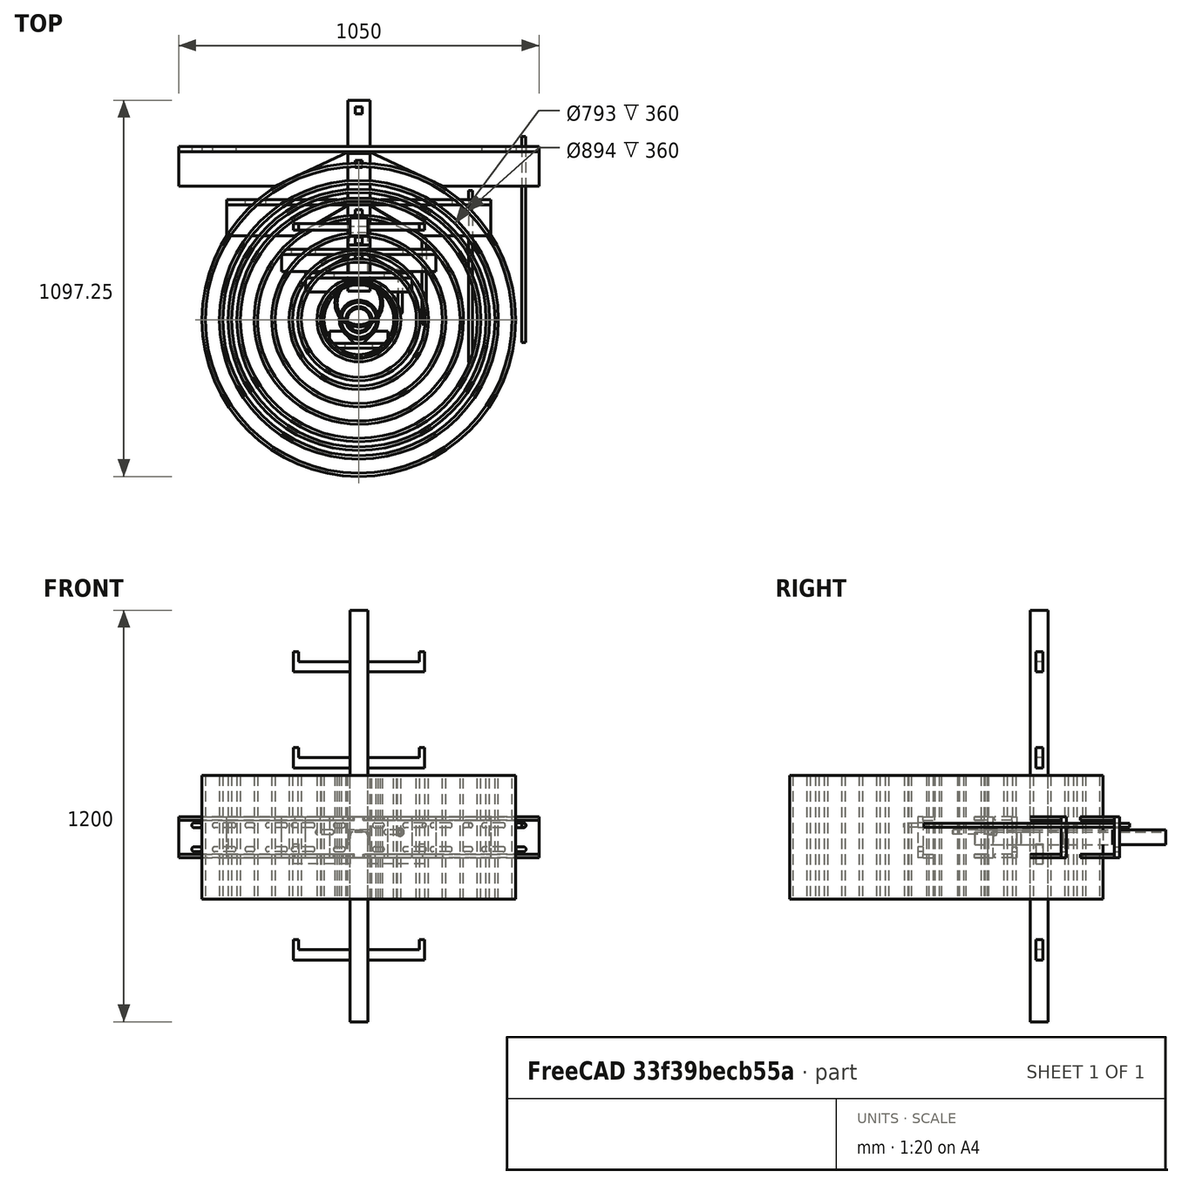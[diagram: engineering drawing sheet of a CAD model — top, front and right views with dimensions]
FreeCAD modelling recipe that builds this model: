
FCSTD DOCUMENT  (FreeCAD 0.21R33771 (Git))
Label: ladder_clamp
License: All rights reserved
LicenseURL: http://en.wikipedia.org/wiki/All_rights_reserved
objects: TechDraw::DrawViewDimension×53, Sketcher::SketchObject×26, Part::Extrusion×25, Part::FeaturePython×17, Part::Feature×15, Part::Cut×12, TechDraw::DrawProjGroupItem×12, App::DocumentObjectGroup×5, TechDraw::DrawSVGTemplate×4, TechDraw::DrawProjGroup×4, TechDraw::DrawViewBalloon×4, TechDraw::DrawViewAnnotation×4, TechDraw::DrawPage×4, Part::Cylinder×3, Fem::ConstraintForce×2, Part::MultiFuse×1, Fem::FemMeshObjectPython×1, Fem::FemSolverObjectPython×1, App::MaterialObjectPython×1, Fem::ConstraintFixed×1, +1 more types
note: 99 computed .brp shape members not serialized (recipe doc carries the construction recipe); baked Part::Feature solids carry a one-line shape summary decoded from their .brp

FEATURE [Part::Feature] BOLTS_part  label="Circular hollow profile 76.1/5.0 l=360.0"
  Placement = pos=(0,0,-120) rot=(0,0,1;0rad)
  shape: bbox 76.1 x 76.1 x 360 mm, 4 faces (baked)
FEATURE [Part::Feature] BOLTS_part001  label="Circular hollow profile 114.3/6.3 l=360.0"
  Placement = pos=(0,0,-120) rot=(0,0,1;0rad)
  shape: bbox 114.3 x 114.3 x 360 mm, 4 faces (baked)
FEATURE [Part::Feature] BOLTS_part002  label="Circular hollow profile 139.7/6.3 l=360.0"
  Placement = pos=(0,49,-120) rot=(0,0,1;0rad)
  shape: bbox 139.7 x 139.7 x 360 mm, 4 faces (baked)
FEATURE [Part::Feature] BOLTS_part003  label="Circular hollow profile 219.1/8.0 l=360.0"
  Placement = pos=(0,0,-120) rot=(0,0,1;0rad)
  shape: bbox 219.1 x 219.1 x 360 mm, 4 faces (baked)
FEATURE [Part::Feature] BOLTS_part004  label="Circular hollow profile 244.5/10.0 l=360.0"
  Placement = pos=(0,0,-120) rot=(0,0,1;0rad)
  shape: bbox 244.5 x 244.5 x 360 mm, 4 faces (baked)
FEATURE [Part::Feature] BOLTS_part005  label="Circular hollow profile 355.6/10.0 l=360.0"
  Placement = pos=(0,0,-120) rot=(0,0,1;0rad)
  shape: bbox 355.6 x 355.6 x 360 mm, 4 faces (baked)
FEATURE [Part::Feature] BOLTS_part006  label="Circular hollow profile 406.4/10.0 l=360.0"
  Placement = pos=(0,0,-120) rot=(0,0,1;0rad)
  shape: bbox 406.4 x 406.4 x 360 mm, 4 faces (baked)
FEATURE [Part::Feature] BOLTS_part007  label="Circular hollow profile 610.0/10.0 l=360.0"
  Placement = pos=(0,0,-120) rot=(0,0,1;0rad)
  shape: bbox 610 x 610 x 360 mm, 4 faces (baked)
FEATURE [Part::Feature] BOLTS_part008  label="Circular hollow profile 914.0/10.0 l=360.0"
  Placement = pos=(0,0,-120) rot=(0,0,1;0rad)
  shape: bbox 914 x 914 x 360 mm, 4 faces (baked)
FEATURE [Sketcher::SketchObject] Sketch
  FullyConstrained = true
  sketch-geometry (10):
    g0: Circle CenterX=0 CenterY=0 CenterZ=0 NormalX=0 NormalY=0 NormalZ=1 AngleXU=0 Radius=57.15
    g1: LineSegment StartX=-47.5 StartY=33.3223 StartZ=0 EndX=-12.5 EndY=68.3223 EndZ=0
    g2: LineSegment StartX=12.5 StartY=68.3223 StartZ=0 EndX=47.5 EndY=33.3223 EndZ=0
    g3: LineSegment StartX=-12.5 StartY=68.3223 StartZ=0 EndX=12.5 EndY=68.3223 EndZ=0
    g4: LineSegment StartX=47.5 StartY=33.3223 StartZ=0 EndX=85 EndY=33.3223 EndZ=0
    g5: LineSegment StartX=85 StartY=33.3223 StartZ=0 EndX=85 EndY=68.3223 EndZ=0
    g6: LineSegment StartX=85 StartY=68.3223 StartZ=0 EndX=12.5 EndY=68.3223 EndZ=0
    g7: LineSegment StartX=-12.5 StartY=68.3223 StartZ=0 EndX=-85 EndY=68.3223 EndZ=0
    g8: LineSegment StartX=-85 StartY=68.3223 StartZ=0 EndX=-85 EndY=33.3223 EndZ=0
    g9: LineSegment StartX=-85 StartY=33.3223 StartZ=0 EndX=-47.5 EndY=33.3223 EndZ=0
  constraints (26):
    c: Coincident(g0,g-1)
    c: Tangent(g1,g0)
    c: Symmetric(g1,g2,g-2)
    c: Symmetric(g1,g2,g-2)
    c: Coincident(g3,g1)
    c: Coincident(g3,g2)
    c: Angle(g-1,g1) = 0.785398
    c: Coincident(g2,g4)
    c: Horizontal(g4)
    c: Coincident(g4,g5)
    c: Vertical(g5)
    c: Coincident(g5,g6)
    c: Coincident(g6,g2)
    c: Horizontal(g6)
    c: Coincident(g1,g7)
    c: Horizontal(g7)
    c: Coincident(g7,g8)
    c: Vertical(g8)
    c: Coincident(g8,g9)
    c: Coincident(g9,g1)
    c: Horizontal(g9)
    c: DistanceY(g5,g5) = 35
    c: Equal(g6,g7)
    c: DistanceX(g6,g6) = 72.5
    c: DistanceX(g7,g5) = 170
    c: Diameter(g0) = 114.3
FEATURE [Part::Extrusion] Extrude  label="Eckblech"
  Base = -> Sketch
  Dir = (0,0,1)
  DirMode = 2
  FaceMakerClass = Part::FaceMakerBullseye
  LengthFwd = 10
  LengthRev = 0
  Solid = true
  Symmetric = false
FEATURE [Part::FeaturePython] Clone  label="Eckblech001"  # Draft clone (typed FeaturePython)
  AttacherType = Attacher::AttachEngine3D
  Fuse = false
  Objects = -> [Extrude]
  Placement = pos=(0,0,110) rot=(0,0,1;0rad)
  Scale = (1,1,1)
FEATURE [Sketcher::SketchObject] Sketch001
  ExternalGeometry = -> [Clone,Extrude]
  FullyConstrained = true
  MapMode = 5
  Placement = pos=(0,68.3223,0) rot=(0,0.707107,0.707107;3.14159rad)
  Support = -> [Extrude]
  sketch-geometry (4):
    g0: LineSegment StartX=-85 StartY=0 StartZ=0 EndX=85 EndY=0 EndZ=0
    g1: LineSegment StartX=85 StartY=0 StartZ=0 EndX=85 EndY=120 EndZ=0
    g2: LineSegment StartX=85 StartY=120 StartZ=0 EndX=-85 EndY=120 EndZ=0
    g3: LineSegment StartX=-85 StartY=120 StartZ=0 EndX=-85 EndY=0 EndZ=0
  constraints (10):
    c: Coincident(g0,g1)
    c: Coincident(g1,g2)
    c: Coincident(g2,g3)
    c: Coincident(g3,g0)
    c: Horizontal(g0)
    c: Horizontal(g2)
    c: Vertical(g1)
    c: Vertical(g3)
    c: Coincident(g0,g-4)
    c: Coincident(g1,g-3)
FEATURE [Part::Extrusion] Extrude001  label="Extrude002"
  Base = -> Sketch001
  Dir = (0,1,-2e-16)
  DirMode = 2
  FaceMakerClass = Part::FaceMakerBullseye
  LengthFwd = 15
  LengthRev = 0
  Solid = true
  Symmetric = false
FEATURE [Sketcher::SketchObject] Sketch002
  ExternalGeometry = -> [Extrude001]
  FullyConstrained = true
  MapMode = 5
  Placement = pos=(0,83.3223,-2e-14) rot=(0,0.707107,0.707107;3.14159rad)
  Support = -> [Extrude001]
  sketch-geometry (13):
    g0: LineSegment StartX=-32.5 StartY=39 StartZ=0 EndX=-32.5 EndY=81 EndZ=0
    g1: LineSegment StartX=-32.5 StartY=81 StartZ=0 EndX=32.5 EndY=81 EndZ=0
    g2: LineSegment StartX=32.5 StartY=81 StartZ=0 EndX=32.5 EndY=39 EndZ=0
    g3: LineSegment StartX=-32.5 StartY=81 StartZ=0 EndX=-85 EndY=120 EndZ=0
    g4: LineSegment StartX=32.5 StartY=81 StartZ=0 EndX=85 EndY=120 EndZ=0
    g5: LineSegment StartX=-16.5 StartY=75.5 StartZ=0 EndX=16.5 EndY=75.5 EndZ=0
    g6: LineSegment StartX=23.89 StartY=69.2796 StartZ=0 EndX=28.5586 EndY=42.3175 EndZ=0
    g7: LineSegment StartX=-23.89 StartY=69.2796 StartZ=0 EndX=-28.5586 EndY=42.3175 EndZ=0
    g8: ArcOfCircle CenterX=32.5 CenterY=43 CenterZ=0 NormalX=0 NormalY=0 NormalZ=1 AngleXU=0 Radius=4 StartAngle=3.31305 EndAngle=4.71239
    g9: ArcOfCircle CenterX=16.5 CenterY=68 CenterZ=0 NormalX=0 NormalY=0 NormalZ=1 AngleXU=0 Radius=7.5 StartAngle=0.171455 EndAngle=1.5708
    g10: ArcOfCircle CenterX=-32.5 CenterY=43 CenterZ=0 NormalX=0 NormalY=0 NormalZ=1 AngleXU=0 Radius=4 StartAngle=4.71239 EndAngle=6.11173
    g11: ArcOfCircle CenterX=-16.5 CenterY=68 CenterZ=0 NormalX=0 NormalY=0 NormalZ=1 AngleXU=0 Radius=7.5 StartAngle=1.5708 EndAngle=2.97014
    g12: LineSegment StartX=-85 StartY=1.42e-14 StartZ=0 EndX=-32.5 EndY=39 EndZ=0
  constraints (35):
    c: Vertical(g0)
    c: Coincident(g0,g1)
    c: Horizontal(g1)
    c: Coincident(g1,g2)
    c: Vertical(g2)
    c: Coincident(g3,g0)
    c: Coincident(g4,g1)
    c: Coincident(g3,g-4)
    c: Coincident(g4,g-3)
    c: Equal(g3,g4)
    c: DistanceX(g1,g1) = 65
    c: DistanceY(g0,g0) = 42
    c: Equal(g0,g2)
    c: PointOnObject(g8,g2)
    c: Coincident(g8,g2)
    c: Coincident(g9,g5)
    c: Vertical(g9,g5)
    c: Tangent(g6,g9) = 1.5708
    c: Tangent(g8,g6) = -1.5708
    c: Symmetric(g5,g5,g-2)
    c: DistanceY(g5,g1) = 5.5
    c: Radius(g9) = 7.5
    c: Radius(g8) = 4
    c: DistanceX(g5,g5) = 33
    c: PointOnObject(g10,g0)
    c: Coincident(g10,g0)
    c: Coincident(g11,g5)
    c: Vertical(g11,g5)
    c: Equal(g9,g11)
    c: Tangent(g11,g7) = -1.5708
    c: Equal(g8,g10)
    c: Tangent(g10,g7) = 1.5708
    c: Coincident(g12,g-4)
    c: Coincident(g12,g0)
    c: Equal(g3,g12)
FEATURE [Part::Extrusion] Extrude002  label="Extrude003"
  Base = -> Sketch002
  Dir = (0,1,-2e-16)
  DirMode = 2
  FaceMakerClass = Part::FaceMakerBullseye
  LengthFwd = 135
  LengthRev = 0
  Solid = true
  Symmetric = false
FEATURE [Sketcher::SketchObject] Sketch003
  ExternalGeometry = -> [Extrude002]
  FullyConstrained = true
  MapMode = 5
  Placement = pos=(0,1.78e-14,81) rot=(0,0,1;0rad)
  Support = -> [Extrude002]
  sketch-geometry (7):
    g0: LineSegment StartX=-10 StartY=198.322 StartZ=0 EndX=10 EndY=198.322 EndZ=0
    g1: LineSegment StartX=10 StartY=198.322 StartZ=0 EndX=10 EndY=178.322 EndZ=0
    g2: LineSegment StartX=10 StartY=178.322 StartZ=0 EndX=-10 EndY=178.322 EndZ=0
    g3: LineSegment StartX=-10 StartY=178.322 StartZ=0 EndX=-10 EndY=198.322 EndZ=0
    g4: LineSegment StartX=-10 StartY=198.322 StartZ=0 EndX=-32.5 EndY=218.322 EndZ=0
    g5: LineSegment StartX=10 StartY=198.322 StartZ=0 EndX=32.5 EndY=218.322 EndZ=0
    g6: LineSegment StartX=10 StartY=188.322 StartZ=0 EndX=32.5 EndY=188.322 EndZ=0
  constraints (19):
    c: Coincident(g0,g1)
    c: Coincident(g1,g2)
    c: Coincident(g2,g3)
    c: Coincident(g3,g0)
    c: Horizontal(g0)
    c: Horizontal(g2)
    c: Vertical(g1)
    c: Vertical(g3)
    c: DistanceX(g2,g2) = 20
    c: DistanceY(g1,g1) = 20
    c: Coincident(g4,g0)
    c: Coincident(g5,g0)
    c: Coincident(g4,g-3)
    c: Coincident(g5,g-3)
    c: Equal(g4,g5)
    c: PointOnObject(g6,g1)
    c: Vertical(g5,g6)
    c: Symmetric(g1,g0,g6)
    c: DistanceY(g6,g5) = 30
FEATURE [Part::Extrusion] Extrude003  label="Extrude004"
  Base = -> Sketch003
  Dir = (0,2e-16,1)
  DirMode = 2
  FaceMakerClass = Part::FaceMakerBullseye
  LengthFwd = 30
  LengthRev = 0
  Solid = true
  Symmetric = true
FEATURE [Part::Cut] Cut  label="U65"
  Base = -> Extrude002
  Refine = true
  Tool = -> Extrude003
FEATURE [Sketcher::SketchObject] Sketch004
  ExternalGeometry = -> [Clone,Extrude]
  FullyConstrained = true
  MapMode = 5
  Placement = pos=(0,68.3223,-1.64e-14) rot=(1,0,0;1.5708rad)
  Support = -> [Extrude001]
  sketch-geometry (19):
    g0: ArcOfCircle CenterX=-67 CenterY=95 CenterZ=0 NormalX=0 NormalY=0 NormalZ=1 AngleXU=0 Radius=7 StartAngle=1.5708 EndAngle=4.71239
    g1: ArcOfCircle CenterX=-47 CenterY=95 CenterZ=0 NormalX=0 NormalY=0 NormalZ=1 AngleXU=0 Radius=7 StartAngle=4.71239 EndAngle=7.85398
    g2: LineSegment StartX=-67 StartY=88 StartZ=0 EndX=-47 EndY=88 EndZ=0
    g3: LineSegment StartX=-67 StartY=102 StartZ=0 EndX=-47 EndY=102 EndZ=0
    g4: ArcOfCircle CenterX=47 CenterY=95 CenterZ=0 NormalX=0 NormalY=0 NormalZ=1 AngleXU=0 Radius=7 StartAngle=1.5708 EndAngle=4.71239
    g5: ArcOfCircle CenterX=67 CenterY=95 CenterZ=0 NormalX=0 NormalY=0 NormalZ=1 AngleXU=0 Radius=7 StartAngle=4.71239 EndAngle=7.85398
    g6: LineSegment StartX=47 StartY=88 StartZ=0 EndX=67 EndY=88 EndZ=0
    g7: LineSegment StartX=47 StartY=102 StartZ=0 EndX=67 EndY=102 EndZ=0
    g8: ArcOfCircle CenterX=-67 CenterY=25 CenterZ=0 NormalX=0 NormalY=0 NormalZ=1 AngleXU=0 Radius=7 StartAngle=1.5708 EndAngle=4.71239
    g9: ArcOfCircle CenterX=-47 CenterY=25 CenterZ=0 NormalX=0 NormalY=0 NormalZ=1 AngleXU=0 Radius=7 StartAngle=4.71239 EndAngle=7.85398
    g10: LineSegment StartX=-67 StartY=18 StartZ=0 EndX=-47 EndY=18 EndZ=0
    g11: LineSegment StartX=-67 StartY=32 StartZ=0 EndX=-47 EndY=32 EndZ=0
    g12: ArcOfCircle CenterX=47 CenterY=25 CenterZ=0 NormalX=0 NormalY=0 NormalZ=1 AngleXU=0 Radius=7 StartAngle=1.5708 EndAngle=4.71239
    g13: ArcOfCircle CenterX=67 CenterY=25 CenterZ=0 NormalX=0 NormalY=0 NormalZ=1 AngleXU=0 Radius=7 StartAngle=4.71239 EndAngle=7.85398
    g14: LineSegment StartX=47 StartY=18 StartZ=0 EndX=67 EndY=18 EndZ=0
    g15: LineSegment StartX=47 StartY=32 StartZ=0 EndX=67 EndY=32 EndZ=0
    g16: LineSegment StartX=-85 StartY=110 StartZ=0 EndX=-67 EndY=95 EndZ=0
    g17: LineSegment StartX=85 StartY=110 StartZ=0 EndX=67 EndY=95 EndZ=0
    g18: LineSegment StartX=-85 StartY=10 StartZ=0 EndX=-67 EndY=25 EndZ=0
  constraints (44):
    c: Tangent(g0,g3) = 1.5708
    c: Tangent(g2,g1) = -1.5708
    c: Tangent(g3,g1) = 1.5708
    c: Equal(g0,g1)
    c: Tangent(g4,g7) = 1.5708
    c: Tangent(g4,g6) = -1.5708
    c: Tangent(g6,g5) = -1.5708
    c: Tangent(g7,g5) = 1.5708
    c: Horizontal(g6)
    c: Equal(g4,g5)
    c: Tangent(g8,g11) = 1.5708
    c: Tangent(g8,g10) = -1.5708
    c: Tangent(g10,g9) = -1.5708
    c: Tangent(g11,g9) = 1.5708
    c: Horizontal(g10)
    c: Equal(g8,g9)
    c: Tangent(g12,g15) = 1.5708
    c: Tangent(g12,g14) = -1.5708
    c: Tangent(g14,g13) = -1.5708
    c: Tangent(g15,g13) = 1.5708
    c: Horizontal(g14)
    c: Equal(g12,g13)
    c: Symmetric(g1,g4,g-2)
    c: Symmetric(g9,g12,g-2)
    c: Vertical(g1,g9)
    c: Equal(g9,g1)
    c: Equal(g1,g4)
    c: Equal(g4,g12)
    c: Equal(g3,g11)
    c: Equal(g11,g7)
    c: Equal(g7,g15)
    c: Diameter(g0) = 14
    c: DistanceX(g3,g3) = 20
    c: Coincident(g16,g-4)
    c: Coincident(g16,g0)
    c: Coincident(g17,g-3)
    c: Coincident(g17,g5)
    c: DistanceY(g8,g0) = 70
    c: Tangent(g0,g2) = -1.5708
    c: DistanceX(g1,g4) = 94
    c: Horizontal(g2)
    c: Coincident(g18,g-6)
    c: Coincident(g18,g8)
    c: Equal(g16,g18)
FEATURE [Part::Extrusion] Extrude004  label="Extrude005"
  Base = -> Sketch004
  Dir = (0,1,0)
  DirMode = 0
  FaceMakerClass = Part::FaceMakerBullseye
  LengthFwd = 50
  LengthRev = 0
  Solid = true
  Symmetric = true
FEATURE [Part::Cut] Cut001
  Base = -> Extrude001
  Refine = true
  Tool = -> Extrude004
FEATURE [Part::FeaturePython] BooleanFragments  # WARN: FeaturePython — macro-defined, semantics opaque (R4)
  Mode = 0
  Objects = -> [Extrude,Clone,Cut001]
  Tolerance = 0
FEATURE [Part::FeaturePython] Clone001  label="BooleanFragments001"  # Draft clone (typed FeaturePython)
  AttacherType = Attacher::AttachEngine3D
  Fuse = false
  Objects = -> [BooleanFragments]
  Placement = pos=(0,0,0) rot=(0,0,1;3.14159rad)
  Scale = (1,1,1)
FEATURE [Sketcher::SketchObject] Sketch005  label="Basis"
  FullyConstrained = true
  sketch-geometry (10):
    g0: Circle CenterX=0 CenterY=0 CenterZ=0 NormalX=0 NormalY=0 NormalZ=1 AngleXU=0 Radius=57.15
    g1: LineSegment StartX=-47.5 StartY=33.3223 StartZ=0 EndX=-12.5 EndY=68.3223 EndZ=0
    g2: LineSegment StartX=12.5 StartY=68.3223 StartZ=0 EndX=47.5 EndY=33.3223 EndZ=0
    g3: LineSegment StartX=-12.5 StartY=68.3223 StartZ=0 EndX=12.5 EndY=68.3223 EndZ=0
    g4: LineSegment StartX=47.5 StartY=33.3223 StartZ=0 EndX=85 EndY=33.3223 EndZ=0
    g5: LineSegment StartX=85 StartY=33.3223 StartZ=0 EndX=85 EndY=68.3223 EndZ=0
    g6: LineSegment StartX=85 StartY=68.3223 StartZ=0 EndX=12.5 EndY=68.3223 EndZ=0
    g7: LineSegment StartX=-12.5 StartY=68.3223 StartZ=0 EndX=-85 EndY=68.3223 EndZ=0
    g8: LineSegment StartX=-85 StartY=68.3223 StartZ=0 EndX=-85 EndY=33.3223 EndZ=0
    g9: LineSegment StartX=-85 StartY=33.3223 StartZ=0 EndX=-47.5 EndY=33.3223 EndZ=0
  constraints (26):
    c: Coincident(g0,g-1)
    c: Tangent(g1,g0)
    c: Symmetric(g1,g2,g-2)
    c: Symmetric(g1,g2,g-2)
    c: Coincident(g3,g1)
    c: Coincident(g3,g2)
    c: Angle(g-1,g1) = 0.785398
    c: Coincident(g2,g4)
    c: Horizontal(g4)
    c: Coincident(g4,g5)
    c: Vertical(g5)
    c: Coincident(g5,g6)
    c: Coincident(g6,g2)
    c: Horizontal(g6)
    c: Coincident(g1,g7)
    c: Horizontal(g7)
    c: Coincident(g7,g8)
    c: Vertical(g8)
    c: Coincident(g8,g9)
    c: Coincident(g9,g1)
    c: Horizontal(g9)
    c: DistanceY(g5,g5) = 35
    c: Equal(g6,g7)
    c: DistanceX(g6,g6) = 72.5
    c: DistanceX(g7,g5) = 170
    c: Diameter(g0) = 114.3
FEATURE [App::DocumentObjectGroup] Group001  label="R76_114"
  Group = -> [Cut,BooleanFragments,Clone001,BOLTS_part,BOLTS_part001,Sketch005]
FEATURE [TechDraw::DrawSVGTemplate] Template
  EditableTexts = AUTHOR_NAME=Thomas Schrader,DN=1,DRAWING_TITLE=Leiterhalterung,FC-DATE=06.05.2021,FC-SC=1:2,FC-SH=X / Y,FC-SI=A3,FreeCAD_DRAWING=Material: Stahl S235,+5 more (map truncated)
  Height = 297
  Orientation = 1
  Width = 420
FEATURE [TechDraw::DrawProjGroupItem] ProjItem  label="Front"
  CoarseView = false
  Direction = (0,1,0)
  Focus = 100
  HardHidden = false
  IsoCount = 0
  IsoHidden = false
  IsoVisible = false
  LockPosition = true
  Perspective = false
  Rotation = 0
  RotationVector = (-1,0,0)
  Scale = 0.5
  ScaleType = 2
  ScrubCount = 0
  SeamHidden = false
  SeamVisible = true
  SmoothHidden = false
  SmoothVisible = true
  Source = -> [Cut,BooleanFragments]
  Type = 0
  X = 0
  XDirection = (-1,0,0)
  Y = 0
FEATURE [TechDraw::DrawProjGroupItem] ProjItem001  label="Left"
  CoarseView = false
  Direction = (1,1e-16,0)
  Focus = 100
  HardHidden = true
  IsoCount = 0
  IsoHidden = false
  IsoVisible = false
  LockPosition = false
  Perspective = false
  Rotation = 0
  RotationVector = (1,0,0)
  Scale = 0.2
  ScaleType = 2
  ScrubCount = 0
  SeamHidden = false
  SeamVisible = true
  SmoothHidden = false
  SmoothVisible = true
  Source = -> [Cut,BooleanFragments]
  Type = 1
  X = 103.75
  XDirection = (-1e-16,1,0)
  Y = 0
FEATURE [TechDraw::DrawProjGroupItem] ProjItem002  label="Top"
  CoarseView = false
  Direction = (0,0,1)
  Focus = 100
  HardHidden = true
  IsoCount = 0
  IsoHidden = false
  IsoVisible = false
  LockPosition = false
  Perspective = false
  Rotation = 0
  RotationVector = (1,0,0)
  Scale = 0.2
  ScaleType = 2
  ScrubCount = 0
  SeamHidden = false
  SeamVisible = true
  SmoothHidden = false
  SmoothVisible = true
  Source = -> [Cut,BooleanFragments]
  Type = 4
  X = 0
  XDirection = (-1,0,0)
  Y = -91.25
FEATURE [TechDraw::DrawProjGroup] ProjGroup
  Anchor = -> ProjItem
  AutoDistribute = true
  LockPosition = false
  ProjectionType = 0
  Rotation = 0
  Scale = 0.5
  ScaleType = 2
  Source = -> [Cut,BooleanFragments]
  Views = -> [ProjItem,ProjItem001,ProjItem002]
  X = 116.09
  Y = 219.887
  spacingX = 15
  spacingY = 15
FEATURE [TechDraw::DrawViewDimension] Dimension
  AngleOverride = false
  Arbitrary = false
  ArbitraryTolerances = false
  EqualTolerance = true
  ExtensionAngle = 0
  FormatSpec = %.1f
  FormatSpecOverTolerance = %+.1f
  FormatSpecUnderTolerance = %+.1f
  Inverted = false
  LineAngle = 0
  LockPosition = false
  MeasureType = 1
  OverTolerance = 0
  References2D = -> [ProjItem002]
  Rotation = 0
  Scale = 0.2
  ScaleType = 2
  TheoreticalExact = false
  Type = 2
  UnderTolerance = 0
  X = -71.0566
  Y = 37.5
FEATURE [TechDraw::DrawViewDimension] Dimension001
  AngleOverride = false
  Arbitrary = false
  ArbitraryTolerances = false
  EqualTolerance = true
  ExtensionAngle = 0
  FormatSpec = %.1f
  FormatSpecOverTolerance = %+.1f
  FormatSpecUnderTolerance = %+.1f
  Inverted = false
  LineAngle = 0
  LockPosition = false
  MeasureType = 1
  OverTolerance = 0
  References2D = -> [ProjItem002]
  Rotation = 0
  Scale = 0.2
  ScaleType = 2
  TheoreticalExact = false
  Type = 2
  UnderTolerance = 0
  X = -64.7644
  Y = 11.2057
FEATURE [TechDraw::DrawViewDimension] Dimension002
  AngleOverride = false
  Arbitrary = false
  ArbitraryTolerances = false
  EqualTolerance = true
  ExtensionAngle = 0
  FormatSpec = %.1f
  FormatSpecOverTolerance = %+.1f
  FormatSpecUnderTolerance = %+.1f
  Inverted = false
  LineAngle = 0
  LockPosition = false
  MeasureType = 1
  OverTolerance = 0
  References2D = -> [ProjItem]
  Rotation = 0
  Scale = 0.2
  ScaleType = 2
  TheoreticalExact = false
  Type = 1
  UnderTolerance = 0
  X = -0.318123
  Y = 46.2243
FEATURE [TechDraw::DrawViewDimension] Dimension003
  AngleOverride = false
  Arbitrary = false
  ArbitraryTolerances = false
  EqualTolerance = true
  ExtensionAngle = 0
  FormatSpec = %.1f
  FormatSpecOverTolerance = %+.1f
  FormatSpecUnderTolerance = %+.1f
  Inverted = false
  LineAngle = 0
  LockPosition = false
  MeasureType = 1
  OverTolerance = 0
  References2D = -> [ProjItem]
  Rotation = 0
  Scale = 0.2
  ScaleType = 2
  TheoreticalExact = false
  Type = 2
  UnderTolerance = 0
  X = -71.4492
  Y = 0.95437
FEATURE [TechDraw::DrawViewDimension] Dimension004
  AngleOverride = false
  Arbitrary = false
  ArbitraryTolerances = false
  EqualTolerance = true
  ExtensionAngle = 0
  FormatSpec = ⌀%.1f
  FormatSpecOverTolerance = %+.1f
  FormatSpecUnderTolerance = %+.1f
  Inverted = false
  LineAngle = 0
  LockPosition = false
  MeasureType = 1
  OverTolerance = 0
  References2D = -> [ProjItem]
  Rotation = 0
  Scale = 0.2
  ScaleType = 2
  TheoreticalExact = false
  Type = 5
  UnderTolerance = 0
  X = 49.0059
  Y = 14.3186
FEATURE [TechDraw::DrawViewDimension] Dimension005
  AngleOverride = false
  Arbitrary = false
  ArbitraryTolerances = false
  EqualTolerance = true
  ExtensionAngle = 0
  FormatSpec = %.1f
  FormatSpecOverTolerance = %+.1f
  FormatSpecUnderTolerance = %+.1f
  Inverted = false
  LineAngle = 0
  LockPosition = false
  MeasureType = 1
  OverTolerance = 0
  References2D = -> [ProjItem]
  Rotation = 0
  Scale = 0.2
  ScaleType = 2
  TheoreticalExact = false
  Type = 1
  UnderTolerance = 0
  X = -28.5
  Y = 7.01313
FEATURE [TechDraw::DrawViewDimension] Dimension006
  AngleOverride = false
  Arbitrary = false
  ArbitraryTolerances = false
  EqualTolerance = true
  ExtensionAngle = 0
  FormatSpec = %.1f
  FormatSpecOverTolerance = %+.1f
  FormatSpecUnderTolerance = %+.1f
  Inverted = false
  LineAngle = 0
  LockPosition = false
  MeasureType = 1
  OverTolerance = 0
  References2D = -> [ProjItem]
  Rotation = 0
  Scale = 0.2
  ScaleType = 2
  TheoreticalExact = false
  Type = 2
  UnderTolerance = 0
  X = -54.6754
  Y = 3.4284
FEATURE [TechDraw::DrawViewDimension] Dimension007
  AngleOverride = false
  Arbitrary = false
  ArbitraryTolerances = false
  EqualTolerance = true
  ExtensionAngle = 0
  FormatSpec = %.1f
  FormatSpecOverTolerance = %+.1f
  FormatSpecUnderTolerance = %+.1f
  Inverted = false
  LineAngle = 0
  LockPosition = false
  MeasureType = 1
  OverTolerance = 0
  References2D = -> [ProjItem]
  Rotation = 0
  Scale = 0.2
  ScaleType = 2
  TheoreticalExact = false
  Type = 1
  UnderTolerance = 0
  X = -0.403341
  Y = -37.2637
FEATURE [TechDraw::DrawViewDimension] Dimension008
  AngleOverride = false
  Arbitrary = false
  ArbitraryTolerances = false
  EqualTolerance = true
  ExtensionAngle = 0
  FormatSpec = %.1f
  FormatSpecOverTolerance = %+.1f
  FormatSpecUnderTolerance = %+.1f
  Inverted = false
  LineAngle = 0
  LockPosition = false
  MeasureType = 1
  OverTolerance = 0
  References2D = -> [ProjItem002]
  Rotation = 0
  Scale = 0.2
  ScaleType = 2
  TheoreticalExact = false
  Type = 1
  UnderTolerance = 0
  X = 32.8723
  Y = -34.6868
FEATURE [TechDraw::DrawViewDimension] Dimension009
  AngleOverride = false
  Arbitrary = false
  ArbitraryTolerances = false
  EqualTolerance = true
  ExtensionAngle = 0
  FormatSpec = %.1f
  FormatSpecOverTolerance = %+.1f
  FormatSpecUnderTolerance = %+.1f
  Inverted = false
  LineAngle = 0
  LockPosition = false
  MeasureType = 1
  OverTolerance = 0
  References2D = -> [ProjItem002]
  Rotation = 0
  Scale = 0.2
  ScaleType = 2
  TheoreticalExact = false
  Type = 2
  UnderTolerance = 0
  X = 19.5011
  Y = -16.5424
FEATURE [TechDraw::DrawViewDimension] Dimension010
  AngleOverride = false
  Arbitrary = false
  ArbitraryTolerances = false
  EqualTolerance = true
  ExtensionAngle = 0
  FormatSpec = %.1f
  FormatSpecOverTolerance = %+.1f
  FormatSpecUnderTolerance = %+.1f
  Inverted = false
  LineAngle = 0
  LockPosition = false
  MeasureType = 1
  OverTolerance = 0
  References2D = -> [ProjItem002]
  Rotation = 0
  Scale = 0.2
  ScaleType = 2
  TheoreticalExact = false
  Type = 2
  UnderTolerance = 0
  X = -50.5722
  Y = 0.025058
FEATURE [TechDraw::DrawViewDimension] Dimension011
  AngleOverride = false
  Arbitrary = false
  ArbitraryTolerances = false
  EqualTolerance = true
  ExtensionAngle = 0
  FormatSpec = %.1f
  FormatSpecOverTolerance = %+.1f
  FormatSpecUnderTolerance = %+.1f
  Inverted = false
  LineAngle = 0
  LockPosition = false
  MeasureType = 1
  OverTolerance = 0
  References2D = -> [ProjItem001]
  Rotation = 0
  Scale = 0.2
  ScaleType = 2
  TheoreticalExact = false
  Type = 1
  UnderTolerance = 0
  X = 12.5684
  Y = 23.4751
FEATURE [TechDraw::DrawViewBalloon] Balloon
  BubbleShape = 0
  EndType = 0
  EndTypeScale = 1
  KinkLength = 5
  LockPosition = false
  OriginX = 82.506
  OriginY = -1.18058
  Rotation = 0
  Scale = 0.2
  ScaleType = 2
  ShapeScale = 1
  SourceView = -> ProjItem001
  Text = 1
  TextWrapLen = -1
  X = 122.506
  Y = 38.8194
FEATURE [TechDraw::DrawViewAnnotation] Annotation
  Font = Arial
  LineSpace = 80
  LockPosition = false
  MaxWidth = -1
  Rotation = 0
  Scale = 0.2
  ScaleType = 2
  Text = U-65
  TextSize = 5
  TextStyle = 0
  X = 299.213
  Y = 237.713
FEATURE [TechDraw::DrawPage] Page  label="Page_R76_R114"
  KeepUpdated = true
  NextBalloonIndex = 2
  ProjectionType = 0
  Template = -> Template
  Views = -> [ProjGroup,Dimension,Dimension001,Dimension002,Dimension003,Dimension004,Dimension005,Dimension006,Dimension007,Dimension008,Dimension009,Dimension010,Dimension011,Balloon,Annotation]
FEATURE [Sketcher::SketchObject] Sketch007
  FullyConstrained = true
  sketch-geometry (10):
    g0: Circle CenterX=0 CenterY=0 CenterZ=0 NormalX=0 NormalY=0 NormalZ=1 AngleXU=0 Radius=109.55
    g1: LineSegment StartX=-74.6259 StartY=81.4822 StartZ=0 EndX=-17.5 EndY=121.482 EndZ=0
    g2: LineSegment StartX=17.5 StartY=121.482 StartZ=0 EndX=74.6259 EndY=81.4822 EndZ=0
    g3: LineSegment StartX=-17.5 StartY=121.482 StartZ=0 EndX=17.5 EndY=121.482 EndZ=0
    g4: LineSegment StartX=74.6259 StartY=81.4822 StartZ=0 EndX=155 EndY=81.4822 EndZ=0
    g5: LineSegment StartX=155 StartY=81.4822 StartZ=0 EndX=155 EndY=121.482 EndZ=0
    g6: LineSegment StartX=155 StartY=121.482 StartZ=0 EndX=17.5 EndY=121.482 EndZ=0
    g7: LineSegment StartX=-17.5 StartY=121.482 StartZ=0 EndX=-155 EndY=121.482 EndZ=0
    g8: LineSegment StartX=-155 StartY=121.482 StartZ=0 EndX=-155 EndY=81.4822 EndZ=0
    g9: LineSegment StartX=-155 StartY=81.4822 StartZ=0 EndX=-74.6259 EndY=81.4822 EndZ=0
  constraints (26):
    c: Coincident(g0,g-1)
    c: Tangent(g1,g0)
    c: Symmetric(g1,g2,g-2)
    c: Symmetric(g1,g2,g-2)
    c: Coincident(g3,g1)
    c: Coincident(g3,g2)
    c: Coincident(g2,g4)
    c: Horizontal(g4)
    c: Coincident(g4,g5)
    c: Vertical(g5)
    c: Coincident(g5,g6)
    c: Coincident(g6,g2)
    c: Horizontal(g6)
    c: Coincident(g1,g7)
    c: Horizontal(g7)
    c: Coincident(g7,g8)
    c: Vertical(g8)
    c: Coincident(g8,g9)
    c: Coincident(g9,g1)
    c: Horizontal(g9)
    c: DistanceY(g5,g5) = 40
    c: Equal(g6,g7)
    c: Diameter(g0) = 219.1
    c: DistanceX(g1,g2) = 35
    c: Angle(g-1,g1) = 0.610865
    c: DistanceX(g7,g5) = 310
FEATURE [Part::Extrusion] Extrude005  label="Eckblech002"
  Base = -> Sketch007
  Dir = (0,0,1)
  DirMode = 2
  FaceMakerClass = Part::FaceMakerBullseye
  LengthFwd = 10
  LengthRev = 0
  Solid = true
  Symmetric = false
FEATURE [Part::FeaturePython] Clone004  label="Eckblech003"  # Draft clone (typed FeaturePython)
  AttacherType = Attacher::AttachEngine3D
  Fuse = false
  Objects = -> [Extrude005]
  Placement = pos=(0,0,110) rot=(0,0,1;0rad)
  Scale = (1,1,1)
FEATURE [Sketcher::SketchObject] Sketch008
  ExternalGeometry = -> [Clone004,Extrude005]
  FullyConstrained = true
  MapMode = 5
  Placement = pos=(0,121.482,0) rot=(0,0.707107,0.707107;3.14159rad)
  Support = -> [Extrude005]
  sketch-geometry (4):
    g0: LineSegment StartX=-155 StartY=0 StartZ=0 EndX=155 EndY=0 EndZ=0
    g1: LineSegment StartX=155 StartY=0 StartZ=0 EndX=155 EndY=120 EndZ=0
    g2: LineSegment StartX=155 StartY=120 StartZ=0 EndX=-155 EndY=120 EndZ=0
    g3: LineSegment StartX=-155 StartY=120 StartZ=0 EndX=-155 EndY=0 EndZ=0
  constraints (10):
    c: Coincident(g0,g1)
    c: Coincident(g1,g2)
    c: Coincident(g2,g3)
    c: Coincident(g3,g0)
    c: Horizontal(g0)
    c: Horizontal(g2)
    c: Vertical(g1)
    c: Vertical(g3)
    c: Coincident(g0,g-4)
    c: Coincident(g1,g-3)
FEATURE [Part::Extrusion] Extrude006
  Base = -> Sketch008
  Dir = (0,1,-2e-16)
  DirMode = 2
  FaceMakerClass = Part::FaceMakerBullseye
  LengthFwd = 15
  LengthRev = 0
  Solid = true
  Symmetric = false
FEATURE [Sketcher::SketchObject] Sketch009
  ExternalGeometry = -> [Extrude006]
  FullyConstrained = true
  MapMode = 5
  Placement = pos=(0,136.482,-3.28e-14) rot=(0,0.707107,0.707107;3.14159rad)
  Support = -> [Extrude006]
  sketch-geometry (11):
    g0: LineSegment StartX=-32.5 StartY=39 StartZ=0 EndX=-32.5 EndY=81 EndZ=0
    g1: LineSegment StartX=-32.5 StartY=81 StartZ=0 EndX=32.5 EndY=81 EndZ=0
    g2: LineSegment StartX=32.5 StartY=81 StartZ=0 EndX=32.5 EndY=39 EndZ=0
    g3: LineSegment StartX=-32.5 StartY=81 StartZ=0 EndX=-155 EndY=120 EndZ=0
    g4: LineSegment StartX=32.5 StartY=81 StartZ=0 EndX=155 EndY=120 EndZ=0
    g5: LineSegment StartX=-26.5 StartY=75.5 StartZ=0 EndX=26.5 EndY=75.5 EndZ=0
    g6: LineSegment StartX=26.5 StartY=75.5 StartZ=0 EndX=26.5 EndY=39 EndZ=0
    g7: LineSegment StartX=-26.5 StartY=75.5 StartZ=0 EndX=-26.5 EndY=39 EndZ=0
    g8: LineSegment StartX=-155 StartY=2.84e-14 StartZ=0 EndX=-32.5 EndY=39 EndZ=0
    g9: LineSegment StartX=-32.5 StartY=39 StartZ=0 EndX=-26.5 EndY=39 EndZ=0
    g10: LineSegment StartX=26.5 StartY=39 StartZ=0 EndX=32.5 EndY=39 EndZ=0
  constraints (29):
    c: Vertical(g0)
    c: Coincident(g0,g1)
    c: Horizontal(g1)
    c: Coincident(g1,g2)
    c: Vertical(g2)
    c: Coincident(g3,g0)
    c: Coincident(g4,g1)
    c: Coincident(g3,g-4)
    c: Coincident(g4,g-3)
    c: Equal(g3,g4)
    c: DistanceX(g1,g1) = 65
    c: DistanceY(g0,g0) = 42
    c: Equal(g0,g2)
    c: Symmetric(g5,g5,g-2)
    c: DistanceY(g5,g1) = 5.5
    c: Coincident(g8,g-4)
    c: Coincident(g8,g0)
    c: Equal(g3,g8)
    c: Vertical(g7)
    c: Vertical(g6)
    c: Coincident(g7,g5)
    c: Coincident(g5,g6)
    c: Coincident(g9,g0)
    c: Coincident(g9,g7)
    c: Horizontal(g9)
    c: Coincident(g10,g6)
    c: Coincident(g10,g2)
    c: Horizontal(g10)
    c: DistanceX(g10,g10) = 6
FEATURE [Part::Extrusion] Extrude007
  Base = -> Sketch009
  Dir = (0,1,-2e-16)
  DirMode = 2
  FaceMakerClass = Part::FaceMakerBullseye
  LengthFwd = 135
  LengthRev = 0
  Solid = true
  Symmetric = false
FEATURE [Sketcher::SketchObject] Sketch006
  ExternalGeometry = -> [Extrude007]
  FullyConstrained = true
  MapMode = 5
  Placement = pos=(0,8.6e-15,39) rot=(1,0,0;3.14159rad)
  Support = -> [Extrude007]
  sketch-geometry (4):
    g0: LineSegment StartX=-10 StartY=-221.482 StartZ=0 EndX=10 EndY=-221.482 EndZ=0
    g1: LineSegment StartX=10 StartY=-221.482 StartZ=0 EndX=10 EndY=-241.482 EndZ=0
    g2: LineSegment StartX=10 StartY=-241.482 StartZ=0 EndX=-10 EndY=-241.482 EndZ=0
    g3: LineSegment StartX=-10 StartY=-241.482 StartZ=0 EndX=-10 EndY=-221.482 EndZ=0
  constraints (11):
    c: Coincident(g0,g1)
    c: Coincident(g1,g2)
    c: Coincident(g2,g3)
    c: Coincident(g3,g0)
    c: Horizontal(g0)
    c: Vertical(g1)
    c: Vertical(g3)
    c: DistanceX(g2,g2) = 20
    c: DistanceY(g1,g1) = 20
    c: Symmetric(g2,g1,g-2)
    c: DistanceY(g-3,g1) = 30
FEATURE [Sketcher::SketchObject] Sketch010
  ExternalGeometry = -> [Clone004,Extrude005]
  FullyConstrained = true
  MapMode = 5
  Placement = pos=(0,121.482,-2.92e-14) rot=(1,0,0;1.5708rad)
  Support = -> [Extrude006]
  sketch-geometry (10):
    g0: ArcOfCircle CenterX=-120 CenterY=75 CenterZ=0 NormalX=0 NormalY=0 NormalZ=1 AngleXU=0 Radius=7 StartAngle=1.5708 EndAngle=4.71239
    g1: ArcOfCircle CenterX=-80 CenterY=75 CenterZ=0 NormalX=0 NormalY=0 NormalZ=1 AngleXU=0 Radius=7 StartAngle=4.71239 EndAngle=7.85398
    g2: LineSegment StartX=-120 StartY=68 StartZ=0 EndX=-80 EndY=68 EndZ=0
    g3: LineSegment StartX=-120 StartY=82 StartZ=0 EndX=-80 EndY=82 EndZ=0
    g4: ArcOfCircle CenterX=80 CenterY=75 CenterZ=0 NormalX=0 NormalY=0 NormalZ=1 AngleXU=0 Radius=7 StartAngle=1.5708 EndAngle=4.71239
    g5: ArcOfCircle CenterX=120 CenterY=75 CenterZ=0 NormalX=0 NormalY=0 NormalZ=1 AngleXU=0 Radius=7 StartAngle=4.71239 EndAngle=7.85398
    g6: LineSegment StartX=80 StartY=68 StartZ=0 EndX=120 EndY=68 EndZ=0
    g7: LineSegment StartX=80 StartY=82 StartZ=0 EndX=120 EndY=82 EndZ=0
    g8: LineSegment StartX=-155 StartY=110 StartZ=0 EndX=-120 EndY=75 EndZ=0
    g9: LineSegment StartX=155 StartY=110 StartZ=0 EndX=120 EndY=75 EndZ=0
  constraints (23):
    c: Tangent(g0,g3) = 1.5708
    c: Tangent(g2,g1) = -1.5708
    c: Tangent(g3,g1) = 1.5708
    c: Equal(g0,g1)
    c: Tangent(g4,g7) = 1.5708
    c: Tangent(g4,g6) = -1.5708
    c: Tangent(g6,g5) = -1.5708
    c: Tangent(g7,g5) = 1.5708
    c: Horizontal(g6)
    c: Equal(g4,g5)
    c: Symmetric(g1,g4,g-2)
    c: Equal(g1,g4)
    c: Diameter(g0) = 14
    c: Coincident(g8,g-4)
    c: Coincident(g8,g0)
    c: Coincident(g9,g-3)
    c: Coincident(g9,g5)
    c: Tangent(g0,g2) = -1.5708
    c: Horizontal(g2)
    c: DistanceX(g1,g4) = 160
    c: Equal(g6,g2)
    c: DistanceX(g2,g2) = 40
    c: DistanceY(g0,g8) = 35
FEATURE [Part::Extrusion] Extrude008
  Base = -> Sketch010
  Dir = (0,1,0)
  DirMode = 0
  FaceMakerClass = Part::FaceMakerBullseye
  LengthFwd = 50
  LengthRev = 0
  Solid = true
  Symmetric = true
FEATURE [Part::Cut] Cut003
  Base = -> Extrude006
  Refine = true
  Tool = -> Extrude008
FEATURE [Part::Extrusion] Extrude009
  Base = -> Sketch006
  Dir = (0,-2e-16,-1)
  DirMode = 2
  FaceMakerClass = Part::FaceMakerBullseye
  LengthFwd = 30
  LengthRev = 0
  Placement = pos=(0,0,39) rot=(0,0,1;0rad)
  Solid = true
  Symmetric = true
FEATURE [Part::Cut] Cut002  label="U067"
  Base = -> Extrude007
  Refine = true
  Tool = -> Extrude009
FEATURE [Part::FeaturePython] BooleanFragments002  label="BooleanFragments003"  # WARN: FeaturePython — macro-defined, semantics opaque (R4)
  Mode = 0
  Objects = -> [Extrude005,Clone004,Cut003]
  Tolerance = 0
FEATURE [Part::FeaturePython] Washer  label="M12-Washer"  # Fasteners workbench fastener (typed FeaturePython)
  Placement = pos=(120,136.482,75) rot=(-1,0,0;1.5708rad)
  diameter = 10
  invert = true
  matchOuter = false
  offset = 0
  type = 0
FEATURE [Part::FeaturePython] Screw  label="M12x120-Screw"  # Fasteners workbench fastener (typed FeaturePython)
  Placement = pos=(120,139.182,75) rot=(-1,0,0;1.5708rad)
  baseObject = -> Washer [Edge1]
  diameter = 11
  invert = false
  leftHanded = false
  length = 13
  lengthCustom = 25
  matchOuter = false
  offset = 0
  thread = false
  type = 14
FEATURE [App::DocumentObjectGroup] Group005  label="R139_219"
  Group = -> [Cut002,BooleanFragments002,BOLTS_part002,BOLTS_part003,Screw,Washer]
FEATURE [Sketcher::SketchObject] Sketch015
  FullyConstrained = true
  sketch-geometry (10):
    g0: Circle CenterX=0 CenterY=0 CenterZ=0 NormalX=0 NormalY=0 NormalZ=1 AngleXU=0 Radius=177.8
    g1: LineSegment StartX=-111.603 StartY=140.872 StartZ=0 EndX=-25 EndY=190.872 EndZ=0
    g2: LineSegment StartX=25 StartY=190.872 StartZ=0 EndX=111.603 EndY=140.872 EndZ=0
    g3: LineSegment StartX=-25 StartY=190.872 StartZ=0 EndX=25 EndY=190.872 EndZ=0
    g4: LineSegment StartX=111.603 StartY=140.872 StartZ=0 EndX=225 EndY=140.872 EndZ=0
    g5: LineSegment StartX=225 StartY=140.872 StartZ=0 EndX=225 EndY=190.872 EndZ=0
    g6: LineSegment StartX=225 StartY=190.872 StartZ=0 EndX=25 EndY=190.872 EndZ=0
    g7: LineSegment StartX=-25 StartY=190.872 StartZ=0 EndX=-225 EndY=190.872 EndZ=0
    g8: LineSegment StartX=-225 StartY=190.872 StartZ=0 EndX=-225 EndY=140.872 EndZ=0
    g9: LineSegment StartX=-225 StartY=140.872 StartZ=0 EndX=-111.603 EndY=140.872 EndZ=0
  constraints (26):
    c: Coincident(g0,g-1)
    c: Tangent(g1,g0)
    c: Symmetric(g1,g2,g-2)
    c: Symmetric(g1,g2,g-2)
    c: Coincident(g3,g1)
    c: Coincident(g3,g2)
    c: Coincident(g2,g4)
    c: Horizontal(g4)
    c: Coincident(g4,g5)
    c: Vertical(g5)
    c: Coincident(g5,g6)
    c: Coincident(g6,g2)
    c: Horizontal(g6)
    c: Coincident(g1,g7)
    c: Horizontal(g7)
    c: Coincident(g7,g8)
    c: Vertical(g8)
    c: Coincident(g8,g9)
    c: Coincident(g9,g1)
    c: Horizontal(g9)
    c: Equal(g6,g7)
    c: Angle(g-1,g1) = 0.523599
    c: Diameter(g0) = 355.6
    c: DistanceY(g5,g5) = 50
    c: DistanceX(g1,g2) = 50
    c: DistanceX(g7,g5) = 450
FEATURE [Part::Extrusion] Extrude010  label="Eckblech005"
  Base = -> Sketch015
  Dir = (0,0,1)
  DirMode = 2
  FaceMakerClass = Part::FaceMakerBullseye
  LengthFwd = 10
  LengthRev = 0
  Solid = true
  Symmetric = false
FEATURE [Part::FeaturePython] Clone005  label="Eckblech004"  # Draft clone (typed FeaturePython)
  AttacherType = Attacher::AttachEngine3D
  Fuse = false
  Objects = -> [Extrude010]
  Placement = pos=(0,0,110) rot=(0,0,1;0rad)
  Scale = (1,1,1)
FEATURE [Sketcher::SketchObject] Sketch012
  ExternalGeometry = -> [Clone005,Extrude010]
  FullyConstrained = true
  MapMode = 5
  Placement = pos=(0,190.872,0) rot=(0,0.707107,0.707107;3.14159rad)
  Support = -> [Extrude010]
  sketch-geometry (4):
    g0: LineSegment StartX=-225 StartY=0 StartZ=0 EndX=225 EndY=0 EndZ=0
    g1: LineSegment StartX=225 StartY=0 StartZ=0 EndX=225 EndY=120 EndZ=0
    g2: LineSegment StartX=225 StartY=120 StartZ=0 EndX=-225 EndY=120 EndZ=0
    g3: LineSegment StartX=-225 StartY=120 StartZ=0 EndX=-225 EndY=0 EndZ=0
  constraints (10):
    c: Coincident(g0,g1)
    c: Coincident(g1,g2)
    c: Coincident(g2,g3)
    c: Coincident(g3,g0)
    c: Horizontal(g0)
    c: Horizontal(g2)
    c: Vertical(g1)
    c: Vertical(g3)
    c: Coincident(g0,g-4)
    c: Coincident(g1,g-3)
FEATURE [Part::Extrusion] Extrude013
  Base = -> Sketch012
  Dir = (0,1,-2e-16)
  DirMode = 2
  FaceMakerClass = Part::FaceMakerBullseye
  LengthFwd = 15
  LengthRev = 0
  Solid = true
  Symmetric = false
FEATURE [Sketcher::SketchObject] Sketch013
  ExternalGeometry = -> [Extrude013]
  FullyConstrained = true
  MapMode = 5
  Placement = pos=(0,205.872,-4.94e-14) rot=(0,0.707107,0.707107;3.14159rad)
  Support = -> [Extrude013]
  sketch-geometry (13):
    g0: LineSegment StartX=-32.5 StartY=39 StartZ=0 EndX=-32.5 EndY=81 EndZ=0
    g1: LineSegment StartX=-32.5 StartY=81 StartZ=0 EndX=32.5 EndY=81 EndZ=0
    g2: LineSegment StartX=32.5 StartY=81 StartZ=0 EndX=32.5 EndY=39 EndZ=0
    g3: LineSegment StartX=-32.5 StartY=81 StartZ=0 EndX=-225 EndY=120 EndZ=0
    g4: LineSegment StartX=32.5 StartY=81 StartZ=0 EndX=225 EndY=120 EndZ=0
    g5: LineSegment StartX=-16.5 StartY=75.5 StartZ=0 EndX=16.5 EndY=75.5 EndZ=0
    g6: LineSegment StartX=23.89 StartY=69.2796 StartZ=0 EndX=28.5586 EndY=42.3175 EndZ=0
    g7: LineSegment StartX=-23.89 StartY=69.2796 StartZ=0 EndX=-28.5586 EndY=42.3175 EndZ=0
    g8: ArcOfCircle CenterX=32.5 CenterY=43 CenterZ=0 NormalX=0 NormalY=0 NormalZ=1 AngleXU=0 Radius=4 StartAngle=3.31305 EndAngle=4.71239
    g9: ArcOfCircle CenterX=16.5 CenterY=68 CenterZ=0 NormalX=0 NormalY=0 NormalZ=1 AngleXU=0 Radius=7.5 StartAngle=0.171455 EndAngle=1.5708
    g10: ArcOfCircle CenterX=-32.5 CenterY=43 CenterZ=0 NormalX=0 NormalY=0 NormalZ=1 AngleXU=0 Radius=4 StartAngle=4.71239 EndAngle=6.11173
    g11: ArcOfCircle CenterX=-16.5 CenterY=68 CenterZ=0 NormalX=0 NormalY=0 NormalZ=1 AngleXU=0 Radius=7.5 StartAngle=1.5708 EndAngle=2.97014
    g12: LineSegment StartX=-225 StartY=2.84e-14 StartZ=0 EndX=-32.5 EndY=39 EndZ=0
  constraints (35):
    c: Vertical(g0)
    c: Coincident(g0,g1)
    c: Horizontal(g1)
    c: Coincident(g1,g2)
    c: Vertical(g2)
    c: Coincident(g3,g0)
    c: Coincident(g4,g1)
    c: Coincident(g3,g-4)
    c: Coincident(g4,g-3)
    c: Equal(g3,g4)
    c: DistanceX(g1,g1) = 65
    c: DistanceY(g0,g0) = 42
    c: Equal(g0,g2)
    c: PointOnObject(g8,g2)
    c: Coincident(g8,g2)
    c: Coincident(g9,g5)
    c: Vertical(g9,g5)
    c: Tangent(g6,g9) = 1.5708
    c: Tangent(g8,g6) = -1.5708
    c: Symmetric(g5,g5,g-2)
    c: DistanceY(g5,g1) = 5.5
    c: Radius(g9) = 7.5
    c: Radius(g8) = 4
    c: DistanceX(g5,g5) = 33
    c: PointOnObject(g10,g0)
    c: Coincident(g10,g0)
    c: Coincident(g11,g5)
    c: Vertical(g11,g5)
    c: Equal(g9,g11)
    c: Tangent(g11,g7) = -1.5708
    c: Equal(g8,g10)
    c: Tangent(g10,g7) = 1.5708
    c: Coincident(g12,g-4)
    c: Coincident(g12,g0)
    c: Equal(g3,g12)
FEATURE [Sketcher::SketchObject] Sketch014
  ExternalGeometry = -> [Clone005,Extrude010]
  FullyConstrained = true
  MapMode = 5
  Placement = pos=(0,190.872,-4.58e-14) rot=(1,0,0;1.5708rad)
  Support = -> [Extrude013]
  sketch-geometry (19):
    g0: ArcOfCircle CenterX=-190 CenterY=95 CenterZ=0 NormalX=0 NormalY=0 NormalZ=1 AngleXU=0 Radius=7 StartAngle=1.5708 EndAngle=4.71239
    g1: ArcOfCircle CenterX=-135 CenterY=95 CenterZ=0 NormalX=0 NormalY=0 NormalZ=1 AngleXU=0 Radius=7 StartAngle=4.71239 EndAngle=7.85398
    g2: LineSegment StartX=-190 StartY=88 StartZ=0 EndX=-135 EndY=88 EndZ=0
    g3: LineSegment StartX=-190 StartY=102 StartZ=0 EndX=-135 EndY=102 EndZ=0
    g4: ArcOfCircle CenterX=135 CenterY=95 CenterZ=0 NormalX=0 NormalY=0 NormalZ=1 AngleXU=0 Radius=7 StartAngle=1.5708 EndAngle=4.71239
    g5: ArcOfCircle CenterX=190 CenterY=95 CenterZ=0 NormalX=0 NormalY=0 NormalZ=1 AngleXU=0 Radius=7 StartAngle=4.71239 EndAngle=7.85398
    g6: LineSegment StartX=135 StartY=88 StartZ=0 EndX=190 EndY=88 EndZ=0
    g7: LineSegment StartX=135 StartY=102 StartZ=0 EndX=190 EndY=102 EndZ=0
    g8: ArcOfCircle CenterX=-190 CenterY=25 CenterZ=0 NormalX=0 NormalY=0 NormalZ=1 AngleXU=0 Radius=7 StartAngle=1.5708 EndAngle=4.71239
    g9: ArcOfCircle CenterX=-135 CenterY=25 CenterZ=0 NormalX=0 NormalY=0 NormalZ=1 AngleXU=0 Radius=7 StartAngle=4.71239 EndAngle=7.85398
    g10: LineSegment StartX=-190 StartY=18 StartZ=0 EndX=-135 EndY=18 EndZ=0
    g11: LineSegment StartX=-190 StartY=32 StartZ=0 EndX=-135 EndY=32 EndZ=0
    g12: ArcOfCircle CenterX=135 CenterY=25 CenterZ=0 NormalX=0 NormalY=0 NormalZ=1 AngleXU=0 Radius=7 StartAngle=1.5708 EndAngle=4.71239
    g13: ArcOfCircle CenterX=190 CenterY=25 CenterZ=0 NormalX=0 NormalY=0 NormalZ=1 AngleXU=0 Radius=7 StartAngle=4.71239 EndAngle=7.85398
    g14: LineSegment StartX=135 StartY=18 StartZ=0 EndX=190 EndY=18 EndZ=0
    g15: LineSegment StartX=135 StartY=32 StartZ=0 EndX=190 EndY=32 EndZ=0
    g16: LineSegment StartX=-225 StartY=110 StartZ=0 EndX=-190 EndY=95 EndZ=0
    g17: LineSegment StartX=225 StartY=110 StartZ=0 EndX=190 EndY=95 EndZ=0
    g18: LineSegment StartX=-225 StartY=10 StartZ=0 EndX=-190 EndY=25 EndZ=0
  constraints (44):
    c: Tangent(g0,g3) = 1.5708
    c: Tangent(g2,g1) = -1.5708
    c: Tangent(g3,g1) = 1.5708
    c: Equal(g0,g1)
    c: Tangent(g4,g7) = 1.5708
    c: Tangent(g4,g6) = -1.5708
    c: Tangent(g6,g5) = -1.5708
    c: Tangent(g7,g5) = 1.5708
    c: Horizontal(g6)
    c: Equal(g4,g5)
    c: Tangent(g8,g11) = 1.5708
    c: Tangent(g8,g10) = -1.5708
    c: Tangent(g10,g9) = -1.5708
    c: Tangent(g11,g9) = 1.5708
    c: Horizontal(g10)
    c: Equal(g8,g9)
    c: Tangent(g12,g15) = 1.5708
    c: Tangent(g12,g14) = -1.5708
    c: Tangent(g14,g13) = -1.5708
    c: Tangent(g15,g13) = 1.5708
    c: Horizontal(g14)
    c: Equal(g12,g13)
    c: Symmetric(g1,g4,g-2)
    c: Symmetric(g9,g12,g-2)
    c: Vertical(g1,g9)
    c: Equal(g9,g1)
    c: Equal(g1,g4)
    c: Equal(g4,g12)
    c: Equal(g3,g11)
    c: Equal(g11,g7)
    c: Equal(g7,g15)
    c: Diameter(g0) = 14
    c: Coincident(g16,g-4)
    c: Coincident(g16,g0)
    c: Coincident(g17,g-3)
    c: Coincident(g17,g5)
    c: DistanceY(g8,g0) = 70
    c: Tangent(g0,g2) = -1.5708
    c: Horizontal(g2)
    c: Coincident(g18,g-6)
    c: Coincident(g18,g8)
    c: Equal(g16,g18)
    c: DistanceX(g11,g11) = 55
    c: DistanceX(g1,g4) = 270
FEATURE [Part::Extrusion] Extrude011
  Base = -> Sketch013
  Dir = (0,1,-2e-16)
  DirMode = 2
  FaceMakerClass = Part::FaceMakerBullseye
  LengthFwd = 135
  LengthRev = 0
  Solid = true
  Symmetric = false
FEATURE [Sketcher::SketchObject] Sketch011
  ExternalGeometry = -> [Extrude011]
  FullyConstrained = true
  MapMode = 5
  Placement = pos=(0,1.78e-14,81) rot=(0,0,1;0rad)
  Support = -> [Extrude011]
  sketch-geometry (7):
    g0: LineSegment StartX=-10 StartY=320.872 StartZ=0 EndX=10 EndY=320.872 EndZ=0
    g1: LineSegment StartX=10 StartY=320.872 StartZ=0 EndX=10 EndY=300.872 EndZ=0
    g2: LineSegment StartX=10 StartY=300.872 StartZ=0 EndX=-10 EndY=300.872 EndZ=0
    g3: LineSegment StartX=-10 StartY=300.872 StartZ=0 EndX=-10 EndY=320.872 EndZ=0
    g4: LineSegment StartX=-10 StartY=320.872 StartZ=0 EndX=-32.5 EndY=340.872 EndZ=0
    g5: LineSegment StartX=10 StartY=320.872 StartZ=0 EndX=32.5 EndY=340.872 EndZ=0
    g6: LineSegment StartX=10 StartY=310.872 StartZ=0 EndX=32.5 EndY=310.872 EndZ=0
  constraints (19):
    c: Coincident(g0,g1)
    c: Coincident(g1,g2)
    c: Coincident(g2,g3)
    c: Coincident(g3,g0)
    c: Horizontal(g0)
    c: Horizontal(g2)
    c: Vertical(g1)
    c: Vertical(g3)
    c: DistanceX(g2,g2) = 20
    c: DistanceY(g1,g1) = 20
    c: Coincident(g4,g0)
    c: Coincident(g5,g0)
    c: Coincident(g4,g-3)
    c: Coincident(g5,g-3)
    c: Equal(g4,g5)
    c: PointOnObject(g6,g1)
    c: Vertical(g5,g6)
    c: Symmetric(g1,g0,g6)
    c: DistanceY(g6,g5) = 30
FEATURE [Part::Extrusion] Extrude012
  Base = -> Sketch011
  Dir = (0,2e-16,1)
  DirMode = 2
  FaceMakerClass = Part::FaceMakerBullseye
  LengthFwd = 30
  LengthRev = 0
  Solid = true
  Symmetric = true
FEATURE [Part::Cut] Cut004  label="U068"
  Base = -> Extrude011
  Refine = true
  Tool = -> Extrude012
FEATURE [Part::Extrusion] Extrude014
  Base = -> Sketch014
  Dir = (0,1,0)
  DirMode = 0
  FaceMakerClass = Part::FaceMakerBullseye
  LengthFwd = 50
  LengthRev = 0
  Solid = true
  Symmetric = true
FEATURE [Part::Cut] Cut005
  Base = -> Extrude013
  Refine = true
  Tool = -> Extrude014
FEATURE [Part::FeaturePython] BooleanFragments003  label="BooleanFragments004"  # WARN: FeaturePython — macro-defined, semantics opaque (R4)
  Mode = 0
  Objects = -> [Extrude010,Clone005,Cut005]
  Tolerance = 0
FEATURE [Part::Cylinder] Cylinder
  Angle = 360
  AttacherType = Attacher::AttachEngine3D
  FirstAngle = 0
  Height = 250
  Placement = pos=(190,236.872,95) rot=(1,0,0;1.5708rad)
  Radius = 6
  SecondAngle = 0
FEATURE [App::DocumentObjectGroup] Group006  label="R244_355"
  Group = -> [Cut004,Cylinder,BooleanFragments003,BOLTS_part004,BOLTS_part005]
FEATURE [TechDraw::DrawSVGTemplate] Template002
  EditableTexts = AUTHOR_NAME=Axians,DN=DN,DRAWING_TITLE=Leiterhalterung,FC-DATE=06.05.2021,FC-REV=REV A,FC-SC=1:2,FC-SH=X / Y,FC-SI=A3,+6 more (map truncated)
  Height = 297
  Orientation = 1
  Width = 420
FEATURE [TechDraw::DrawProjGroupItem] ProjItem006  label="Front002"
  CoarseView = false
  Direction = (0,1,0)
  Focus = 100
  HardHidden = true
  IsoCount = 0
  IsoHidden = false
  IsoVisible = false
  LockPosition = true
  Perspective = false
  Rotation = 0
  RotationVector = (-1,0,0)
  Scale = 0.5
  ScaleType = 2
  ScrubCount = 0
  SeamHidden = false
  SeamVisible = true
  SmoothHidden = false
  SmoothVisible = true
  Source = -> [Cut004,BooleanFragments003]
  Type = 0
  X = 0
  XDirection = (-1,0,0)
  Y = 0
FEATURE [TechDraw::DrawProjGroupItem] ProjItem007  label="Left002"
  CoarseView = false
  Direction = (1,1e-16,0)
  Focus = 100
  HardHidden = true
  IsoCount = 0
  IsoHidden = false
  IsoVisible = false
  LockPosition = false
  Perspective = false
  Rotation = 0
  RotationVector = (1,0,0)
  Scale = 0.5
  ScaleType = 2
  ScrubCount = 0
  SeamHidden = false
  SeamVisible = true
  SmoothHidden = false
  SmoothVisible = true
  Source = -> [Cut004,BooleanFragments003]
  Type = 1
  X = 177.5
  XDirection = (-1e-16,1,0)
  Y = 0
FEATURE [TechDraw::DrawProjGroupItem] ProjItem008  label="Top002"
  CoarseView = false
  Direction = (0,0,1)
  Focus = 100
  HardHidden = true
  IsoCount = 0
  IsoHidden = false
  IsoVisible = false
  LockPosition = false
  Perspective = false
  Rotation = 0
  RotationVector = (1,0,0)
  Scale = 0.5
  ScaleType = 2
  ScrubCount = 0
  SeamHidden = false
  SeamVisible = true
  SmoothHidden = false
  SmoothVisible = true
  Source = -> [Cut004,BooleanFragments003]
  Type = 4
  X = 0
  XDirection = (-1,0,0)
  Y = -95
FEATURE [TechDraw::DrawProjGroup] ProjGroup002
  Anchor = -> ProjItem006
  AutoDistribute = true
  LockPosition = false
  ProjectionType = 0
  Rotation = 0
  Scale = 0.5
  ScaleType = 2
  Source = -> [Cut004,BooleanFragments003]
  Views = -> [ProjItem006,ProjItem007,ProjItem008]
  X = 147.335
  Y = 234.318
  spacingX = 15
  spacingY = 15
FEATURE [TechDraw::DrawViewBalloon] Balloon002
  BubbleShape = 0
  EndType = 0
  EndTypeScale = 1
  KinkLength = 5
  LockPosition = false
  OriginX = 21.878
  OriginY = -87.9268
  Rotation = 0
  Scale = 0.2
  ScaleType = 2
  ShapeScale = 1
  SourceView = -> ProjItem008
  Text = 1
  TextWrapLen = -1
  X = 61.878
  Y = -47.9268
FEATURE [TechDraw::DrawViewAnnotation] Annotation002
  Font = Arial
  LineSpace = 80
  LockPosition = false
  MaxWidth = -1
  Rotation = 0
  Scale = 0.2
  ScaleType = 2
  Text = U-65
  TextSize = 5
  TextStyle = 0
  X = 186.77
  Y = 97.0772
FEATURE [TechDraw::DrawViewDimension] Dimension024
  AngleOverride = false
  Arbitrary = false
  ArbitraryTolerances = false
  EqualTolerance = true
  ExtensionAngle = 0
  FormatSpec = %.1f
  FormatSpecOverTolerance = %+.1f
  FormatSpecUnderTolerance = %+.1f
  Inverted = false
  LineAngle = 0
  LockPosition = false
  MeasureType = 1
  OverTolerance = 0
  References2D = -> [ProjItem006]
  Rotation = 0
  Scale = 0.2
  ScaleType = 2
  TheoreticalExact = false
  Type = 1
  UnderTolerance = 0
  X = 0.402439
  Y = 39.6585
FEATURE [TechDraw::DrawViewDimension] Dimension025
  AngleOverride = false
  Arbitrary = false
  ArbitraryTolerances = false
  EqualTolerance = true
  ExtensionAngle = 0
  FormatSpec = %.1f
  FormatSpecOverTolerance = %+.1f
  FormatSpecUnderTolerance = %+.1f
  Inverted = false
  LineAngle = 0
  LockPosition = false
  MeasureType = 1
  OverTolerance = 0
  References2D = -> [ProjItem006]
  Rotation = 0
  Scale = 0.2
  ScaleType = 2
  TheoreticalExact = false
  Type = 2
  UnderTolerance = 0
  X = -120.146
  Y = -1.20732
FEATURE [TechDraw::DrawViewDimension] Dimension026
  AngleOverride = false
  Arbitrary = false
  ArbitraryTolerances = false
  EqualTolerance = true
  ExtensionAngle = 0
  FormatSpec = %.1f
  FormatSpecOverTolerance = %+.1f
  FormatSpecUnderTolerance = %+.1f
  Inverted = false
  LineAngle = 0
  LockPosition = false
  MeasureType = 1
  OverTolerance = 0
  References2D = -> [ProjItem008]
  Rotation = 0
  Scale = 0.2
  ScaleType = 2
  TheoreticalExact = false
  Type = 6
  UnderTolerance = 0
  X = 88.7841
  Y = 60.3659
FEATURE [TechDraw::DrawViewDimension] Dimension027
  AngleOverride = false
  Arbitrary = false
  ArbitraryTolerances = false
  EqualTolerance = true
  ExtensionAngle = 0
  FormatSpec = %.1f
  FormatSpecOverTolerance = %+.1f
  FormatSpecUnderTolerance = %+.1f
  Inverted = false
  LineAngle = 0
  LockPosition = false
  MeasureType = 1
  OverTolerance = 0
  References2D = -> [ProjItem008]
  Rotation = 0
  Scale = 0.2
  ScaleType = 2
  TheoreticalExact = false
  Type = 2
  UnderTolerance = 0
  X = 130.207
  Y = 37.5
FEATURE [TechDraw::DrawViewDimension] Dimension028
  AngleOverride = false
  Arbitrary = false
  ArbitraryTolerances = false
  EqualTolerance = true
  ExtensionAngle = 0
  FormatSpec = %.1f
  FormatSpecOverTolerance = %+.1f
  FormatSpecUnderTolerance = %+.1f
  Inverted = false
  LineAngle = 0
  LockPosition = false
  MeasureType = 1
  OverTolerance = 0
  References2D = -> [ProjItem008]
  Rotation = 0
  Scale = 0.2
  ScaleType = 2
  TheoreticalExact = false
  Type = 2
  UnderTolerance = 0
  X = 121.354
  Y = 5.55488
FEATURE [TechDraw::DrawViewDimension] Dimension029
  AngleOverride = false
  Arbitrary = false
  ArbitraryTolerances = false
  EqualTolerance = true
  ExtensionAngle = 0
  FormatSpec = %.1f
  FormatSpecOverTolerance = %+.1f
  FormatSpecUnderTolerance = %+.1f
  Inverted = false
  LineAngle = 0
  LockPosition = false
  MeasureType = 1
  OverTolerance = 0
  References2D = -> [ProjItem007]
  Rotation = 0
  Scale = 0.2
  ScaleType = 2
  TheoreticalExact = false
  Type = 2
  UnderTolerance = 0
  X = -42.431
  Y = 40.6973
FEATURE [TechDraw::DrawViewDimension] Dimension030
  AngleOverride = false
  Arbitrary = false
  ArbitraryTolerances = false
  EqualTolerance = true
  ExtensionAngle = 0
  FormatSpec = %.1f
  FormatSpecOverTolerance = %+.1f
  FormatSpecUnderTolerance = %+.1f
  Inverted = false
  LineAngle = 0
  LockPosition = false
  MeasureType = 1
  OverTolerance = 0
  References2D = -> [ProjItem007]
  Rotation = 0
  Scale = 0.2
  ScaleType = 2
  TheoreticalExact = false
  Type = 1
  UnderTolerance = 0
  X = 13.311
  Y = 46.1354
FEATURE [TechDraw::DrawViewDimension] Dimension031
  AngleOverride = false
  Arbitrary = false
  ArbitraryTolerances = false
  EqualTolerance = true
  ExtensionAngle = 0
  FormatSpec = %.1f
  FormatSpecOverTolerance = %+.1f
  FormatSpecUnderTolerance = %+.1f
  Inverted = false
  LineAngle = 0
  LockPosition = false
  MeasureType = 1
  OverTolerance = 0
  References2D = -> [ProjItem008]
  Rotation = 0
  Scale = 0.2
  ScaleType = 2
  TheoreticalExact = false
  Type = 1
  UnderTolerance = 0
  X = 0.367375
  Y = 65.0439
FEATURE [TechDraw::DrawViewDimension] Dimension032
  AngleOverride = false
  Arbitrary = false
  ArbitraryTolerances = false
  EqualTolerance = true
  ExtensionAngle = 0
  FormatSpec = %.1f
  FormatSpecOverTolerance = %+.1f
  FormatSpecUnderTolerance = %+.1f
  Inverted = false
  LineAngle = 0
  LockPosition = false
  MeasureType = 1
  OverTolerance = 0
  References2D = -> [ProjItem008]
  Rotation = 0
  Scale = 0.2
  ScaleType = 2
  TheoreticalExact = false
  Type = 1
  UnderTolerance = 0
  X = -60.8232
  Y = 64.4055
FEATURE [TechDraw::DrawPage] Page002  label="Page_R244_355"
  KeepUpdated = true
  NextBalloonIndex = 2
  ProjectionType = 0
  Template = -> Template002
  Views = -> [ProjGroup002,Balloon002,Annotation002,Dimension024,Dimension025,Dimension026,Dimension027,Dimension028,Dimension029,Dimension030,Dimension031,Dimension032]
FEATURE [Part::Cylinder] Cylinder001
  Angle = 360
  AttacherType = Attacher::AttachEngine3D
  FirstAngle = 0
  Height = 500
  Placement = pos=(325,376.863,95) rot=(1,0,0;1.5708rad)
  Radius = 6
  SecondAngle = 0
FEATURE [Sketcher::SketchObject] Sketch020
  FullyConstrained = true
  sketch-geometry (10):
    g0: Circle CenterX=0 CenterY=0 CenterZ=0 NormalX=0 NormalY=0 NormalZ=1 AngleXU=0 Radius=305
    g1: LineSegment StartX=-185.885 StartY=244.863 StartZ=0 EndX=-30 EndY=334.863 EndZ=0
    g2: LineSegment StartX=30 StartY=334.863 StartZ=0 EndX=185.885 EndY=244.863 EndZ=0
    g3: LineSegment StartX=-30 StartY=334.863 StartZ=0 EndX=30 EndY=334.863 EndZ=0
    g4: LineSegment StartX=185.885 StartY=244.863 StartZ=0 EndX=385 EndY=244.863 EndZ=0
    g5: LineSegment StartX=385 StartY=244.863 StartZ=0 EndX=385 EndY=334.863 EndZ=0
    g6: LineSegment StartX=385 StartY=334.863 StartZ=0 EndX=30 EndY=334.863 EndZ=0
    g7: LineSegment StartX=-30 StartY=334.863 StartZ=0 EndX=-385 EndY=334.863 EndZ=0
    g8: LineSegment StartX=-385 StartY=334.863 StartZ=0 EndX=-385 EndY=244.863 EndZ=0
    g9: LineSegment StartX=-385 StartY=244.863 StartZ=0 EndX=-185.885 EndY=244.863 EndZ=0
  constraints (26):
    c: Coincident(g0,g-1)
    c: Tangent(g1,g0)
    c: Symmetric(g1,g2,g-2)
    c: Symmetric(g1,g2,g-2)
    c: Coincident(g3,g1)
    c: Coincident(g3,g2)
    c: Coincident(g2,g4)
    c: Horizontal(g4)
    c: Coincident(g4,g5)
    c: Vertical(g5)
    c: Coincident(g5,g6)
    c: Coincident(g6,g2)
    c: Horizontal(g6)
    c: Coincident(g1,g7)
    c: Horizontal(g7)
    c: Coincident(g7,g8)
    c: Vertical(g8)
    c: Coincident(g8,g9)
    c: Coincident(g9,g1)
    c: Horizontal(g9)
    c: Equal(g6,g7)
    c: Angle(g-1,g1) = 0.523599
    c: Diameter(g0) = 610
    c: DistanceX(g3,g3) = 60
    c: DistanceY(g5,g5) = 90
    c: DistanceX(g7,g5) = 770
FEATURE [Part::Extrusion] Extrude019  label="Eckblech006"
  Base = -> Sketch020
  Dir = (0,0,1)
  DirMode = 2
  FaceMakerClass = Part::FaceMakerBullseye
  LengthFwd = 10
  LengthRev = 0
  Solid = true
  Symmetric = false
FEATURE [Part::FeaturePython] Clone006  label="Eckblech007"  # Draft clone (typed FeaturePython)
  AttacherType = Attacher::AttachEngine3D
  Fuse = false
  Objects = -> [Extrude019]
  Placement = pos=(0,0,110) rot=(0,0,1;0rad)
  Scale = (1,1,1)
FEATURE [Sketcher::SketchObject] Sketch016
  ExternalGeometry = -> [Clone006,Extrude019]
  FullyConstrained = true
  MapMode = 5
  Placement = pos=(0,334.863,0) rot=(0,0.707107,0.707107;3.14159rad)
  Support = -> [Extrude019]
  sketch-geometry (4):
    g0: LineSegment StartX=-385 StartY=0 StartZ=0 EndX=385 EndY=0 EndZ=0
    g1: LineSegment StartX=385 StartY=0 StartZ=0 EndX=385 EndY=120 EndZ=0
    g2: LineSegment StartX=385 StartY=120 StartZ=0 EndX=-385 EndY=120 EndZ=0
    g3: LineSegment StartX=-385 StartY=120 StartZ=0 EndX=-385 EndY=0 EndZ=0
  constraints (10):
    c: Coincident(g0,g1)
    c: Coincident(g1,g2)
    c: Coincident(g2,g3)
    c: Coincident(g3,g0)
    c: Horizontal(g0)
    c: Horizontal(g2)
    c: Vertical(g1)
    c: Vertical(g3)
    c: Coincident(g0,g-4)
    c: Coincident(g1,g-3)
FEATURE [Part::Extrusion] Extrude015
  Base = -> Sketch016
  Dir = (0,1,-2e-16)
  DirMode = 2
  FaceMakerClass = Part::FaceMakerBullseye
  LengthFwd = 15
  LengthRev = 0
  Solid = true
  Symmetric = false
FEATURE [Sketcher::SketchObject] Sketch018
  ExternalGeometry = -> [Clone006,Extrude019]
  FullyConstrained = true
  MapMode = 5
  Placement = pos=(0,334.863,0) rot=(1,0,0;1.5708rad)
  Support = -> [Extrude015]
  sketch-geometry (36):
    g0: ArcOfCircle CenterX=-265 CenterY=95 CenterZ=0 NormalX=0 NormalY=0 NormalZ=1 AngleXU=0 Radius=7 StartAngle=1.5708 EndAngle=4.71239
    g1: ArcOfCircle CenterX=-215 CenterY=95 CenterZ=0 NormalX=0 NormalY=0 NormalZ=1 AngleXU=0 Radius=7 StartAngle=4.71239 EndAngle=7.85398
    g2: LineSegment StartX=-265 StartY=88 StartZ=0 EndX=-215 EndY=88 EndZ=0
    g3: LineSegment StartX=-265 StartY=102 StartZ=0 EndX=-215 EndY=102 EndZ=0
    g4: ArcOfCircle CenterX=215 CenterY=95 CenterZ=0 NormalX=0 NormalY=0 NormalZ=1 AngleXU=0 Radius=7 StartAngle=1.5708 EndAngle=4.71239
    g5: ArcOfCircle CenterX=265 CenterY=95 CenterZ=0 NormalX=0 NormalY=0 NormalZ=1 AngleXU=0 Radius=7 StartAngle=4.71239 EndAngle=7.85398
    g6: LineSegment StartX=215 StartY=88 StartZ=0 EndX=265 EndY=88 EndZ=0
    g7: LineSegment StartX=215 StartY=102 StartZ=0 EndX=265 EndY=102 EndZ=0
    g8: ArcOfCircle CenterX=-265 CenterY=25 CenterZ=0 NormalX=0 NormalY=0 NormalZ=1 AngleXU=0 Radius=7 StartAngle=1.5708 EndAngle=4.71239
    g9: ArcOfCircle CenterX=-215 CenterY=25 CenterZ=0 NormalX=0 NormalY=0 NormalZ=1 AngleXU=0 Radius=7 StartAngle=4.71239 EndAngle=7.85398
    g10: LineSegment StartX=-265 StartY=18 StartZ=0 EndX=-215 EndY=18 EndZ=0
    g11: LineSegment StartX=-265 StartY=32 StartZ=0 EndX=-215 EndY=32 EndZ=0
    g12: ArcOfCircle CenterX=215 CenterY=25 CenterZ=0 NormalX=0 NormalY=0 NormalZ=1 AngleXU=0 Radius=7 StartAngle=1.5708 EndAngle=4.71239
    g13: ArcOfCircle CenterX=265 CenterY=25 CenterZ=0 NormalX=0 NormalY=0 NormalZ=1 AngleXU=0 Radius=7 StartAngle=4.71239 EndAngle=7.85398
    g14: LineSegment StartX=215 StartY=18 StartZ=0 EndX=265 EndY=18 EndZ=0
    g15: LineSegment StartX=215 StartY=32 StartZ=0 EndX=265 EndY=32 EndZ=0
    g16: LineSegment StartX=-385 StartY=110 StartZ=0 EndX=-265 EndY=95 EndZ=0
    g17: LineSegment StartX=385 StartY=110 StartZ=0 EndX=265 EndY=95 EndZ=0
    g18: LineSegment StartX=-385 StartY=10 StartZ=0 EndX=-265 EndY=25 EndZ=0
    g19: ArcOfCircle CenterX=-265 CenterY=95 CenterZ=0 NormalX=0 NormalY=0 NormalZ=1 AngleXU=0 Radius=7 StartAngle=2e-16 EndAngle=1.5708
    g20: ArcOfCircle CenterX=-325 CenterY=95 CenterZ=0 NormalX=0 NormalY=0 NormalZ=1 AngleXU=0 Radius=7 StartAngle=1.5708 EndAngle=4.71239
    g21: ArcOfCircle CenterX=-310 CenterY=95 CenterZ=0 NormalX=0 NormalY=0 NormalZ=1 AngleXU=0 Radius=7 StartAngle=4.71239 EndAngle=7.85398
    g22: LineSegment StartX=-325 StartY=88 StartZ=0 EndX=-310 EndY=88 EndZ=0
    g23: LineSegment StartX=-325 StartY=102 StartZ=0 EndX=-310 EndY=102 EndZ=0
    g24: ArcOfCircle CenterX=-325 CenterY=25 CenterZ=0 NormalX=0 NormalY=0 NormalZ=1 AngleXU=0 Radius=7 StartAngle=1.5708 EndAngle=4.71239
    g25: ArcOfCircle CenterX=-310 CenterY=25 CenterZ=0 NormalX=0 NormalY=0 NormalZ=1 AngleXU=0 Radius=7 StartAngle=4.71239 EndAngle=7.85398
    g26: LineSegment StartX=-325 StartY=18 StartZ=0 EndX=-310 EndY=18 EndZ=0
    g27: LineSegment StartX=-325 StartY=32 StartZ=0 EndX=-310 EndY=32 EndZ=0
    g28: ArcOfCircle CenterX=310 CenterY=95 CenterZ=0 NormalX=0 NormalY=0 NormalZ=1 AngleXU=0 Radius=7 StartAngle=1.5708 EndAngle=4.71239
    g29: ArcOfCircle CenterX=325 CenterY=95 CenterZ=0 NormalX=0 NormalY=0 NormalZ=1 AngleXU=0 Radius=7 StartAngle=4.71239 EndAngle=7.85398
    g30: LineSegment StartX=310 StartY=88 StartZ=0 EndX=325 EndY=88 EndZ=0
    g31: LineSegment StartX=310 StartY=102 StartZ=0 EndX=325 EndY=102 EndZ=0
    g32: ArcOfCircle CenterX=310 CenterY=25 CenterZ=0 NormalX=0 NormalY=0 NormalZ=1 AngleXU=0 Radius=7 StartAngle=1.5708 EndAngle=4.71239
    g33: ArcOfCircle CenterX=325 CenterY=25 CenterZ=0 NormalX=0 NormalY=0 NormalZ=1 AngleXU=0 Radius=7 StartAngle=4.71239 EndAngle=7.85398
    g34: LineSegment StartX=310 StartY=18 StartZ=0 EndX=325 EndY=18 EndZ=0
    g35: LineSegment StartX=310 StartY=32 StartZ=0 EndX=325 EndY=32 EndZ=0
  constraints (85):
    c: Tangent(g0,g3) = 1.5708
    c: Tangent(g2,g1) = -1.5708
    c: Tangent(g3,g1) = 1.5708
    c: Equal(g0,g1)
    c: Tangent(g4,g7) = 1.5708
    c: Tangent(g4,g6) = -1.5708
    c: Tangent(g6,g5) = -1.5708
    c: Tangent(g7,g5) = 1.5708
    c: Horizontal(g6)
    c: Equal(g4,g5)
    c: Tangent(g8,g11) = 1.5708
    c: Tangent(g8,g10) = -1.5708
    c: Tangent(g10,g9) = -1.5708
    c: Tangent(g11,g9) = 1.5708
    c: Horizontal(g10)
    c: Equal(g8,g9)
    c: Tangent(g12,g15) = 1.5708
    c: Tangent(g12,g14) = -1.5708
    c: Tangent(g14,g13) = -1.5708
    c: Tangent(g15,g13) = 1.5708
    c: Horizontal(g14)
    c: Equal(g12,g13)
    c: Symmetric(g1,g4,g-2)
    c: Symmetric(g9,g12,g-2)
    c: Vertical(g1,g9)
    c: Equal(g9,g1)
    c: Equal(g1,g4)
    c: Equal(g4,g12)
    c: Equal(g3,g11)
    c: Equal(g11,g7)
    c: Equal(g7,g15)
    c: Diameter(g0) = 14
    c: Coincident(g16,g-4)
    c: Coincident(g16,g0)
    c: Coincident(g17,g-3)
    c: Coincident(g17,g5)
    c: DistanceY(g8,g0) = 70
    c: Tangent(g0,g2) = -1.5708
    c: Horizontal(g2)
    c: Coincident(g18,g-6)
    c: Coincident(g18,g8)
    c: Equal(g16,g18)
    c: Coincident(g19,g0)
    c: Coincident(g19,g0)
    c: Horizontal(g19,g0)
    c: DistanceX(g3,g3) = 50
    c: DistanceX(g1,g4) = 430
    c: Tangent(g20,g23) = 1.5708
    c: Tangent(g20,g22) = -1.5708
    c: Tangent(g22,g21) = -1.5708
    c: Tangent(g23,g21) = 1.5708
    c: Horizontal(g22)
    c: Equal(g20,g21)
    c: Tangent(g24,g27) = 1.5708
    c: Tangent(g24,g26) = -1.5708
    c: Tangent(g26,g25) = -1.5708
    c: Tangent(g27,g25) = 1.5708
    c: Horizontal(g26)
    c: Equal(g24,g25)
    c: Tangent(g28,g31) = 1.5708
    c: Tangent(g28,g30) = -1.5708
    c: Tangent(g30,g29) = -1.5708
    c: Tangent(g31,g29) = 1.5708
    c: Horizontal(g30)
    c: Equal(g28,g29)
    c: Tangent(g32,g35) = 1.5708
    c: Tangent(g32,g34) = -1.5708
    c: Tangent(g34,g33) = -1.5708
    c: Tangent(g35,g33) = 1.5708
    c: Horizontal(g34)
    c: Equal(g32,g33)
    c: Equal(g22,g27)
    c: Equal(g27,g30)
    c: Equal(g30,g35)
    c: Equal(g0,g21)
    c: Equal(g21,g25)
    c: Equal(g25,g28)
    c: Equal(g28,g32)
    c: Symmetric(g28,g21,g-2)
    c: Horizontal(g21,g0)
    c: Symmetric(g32,g25,g-2)
    c: Vertical(g21,g25)
    c: DistanceX(g22,g22) = 15
    c: Horizontal(g25,g8)
    c: DistanceX(g13,g32) = 45
FEATURE [Part::Extrusion] Extrude018
  Base = -> Sketch018
  Dir = (0,1,0)
  DirMode = 0
  FaceMakerClass = Part::FaceMakerBullseye
  LengthFwd = 50
  LengthRev = 0
  Solid = true
  Symmetric = true
FEATURE [Part::Cut] Cut007
  Base = -> Extrude015
  Refine = true
  Tool = -> Extrude018
FEATURE [Part::FeaturePython] BooleanFragments004  label="BooleanFragments005"  # WARN: FeaturePython — macro-defined, semantics opaque (R4)
  Mode = 0
  Objects = -> [Extrude019,Clone006,Cut007]
  Tolerance = 0
FEATURE [Sketcher::SketchObject] Sketch019
  ExternalGeometry = -> [Extrude015]
  FullyConstrained = true
  MapMode = 5
  Placement = pos=(0,349.863,0) rot=(0,0.707107,0.707107;3.14159rad)
  Support = -> [Extrude015]
  sketch-geometry (13):
    g0: LineSegment StartX=-32.5 StartY=39 StartZ=0 EndX=-32.5 EndY=81 EndZ=0
    g1: LineSegment StartX=-32.5 StartY=81 StartZ=0 EndX=32.5 EndY=81 EndZ=0
    g2: LineSegment StartX=32.5 StartY=81 StartZ=0 EndX=32.5 EndY=39 EndZ=0
    g3: LineSegment StartX=-32.5 StartY=81 StartZ=0 EndX=-385 EndY=120 EndZ=0
    g4: LineSegment StartX=32.5 StartY=81 StartZ=0 EndX=385 EndY=120 EndZ=0
    g5: LineSegment StartX=-16.5 StartY=75.5 StartZ=0 EndX=16.5 EndY=75.5 EndZ=0
    g6: LineSegment StartX=23.89 StartY=69.2796 StartZ=0 EndX=28.5586 EndY=42.3175 EndZ=0
    g7: LineSegment StartX=-23.89 StartY=69.2796 StartZ=0 EndX=-28.5586 EndY=42.3175 EndZ=0
    g8: ArcOfCircle CenterX=32.5 CenterY=43 CenterZ=0 NormalX=0 NormalY=0 NormalZ=1 AngleXU=0 Radius=4 StartAngle=3.31305 EndAngle=4.71239
    g9: ArcOfCircle CenterX=16.5 CenterY=68 CenterZ=0 NormalX=0 NormalY=0 NormalZ=1 AngleXU=0 Radius=7.5 StartAngle=0.171455 EndAngle=1.5708
    g10: ArcOfCircle CenterX=-32.5 CenterY=43 CenterZ=0 NormalX=0 NormalY=0 NormalZ=1 AngleXU=0 Radius=4 StartAngle=4.71239 EndAngle=6.11173
    g11: ArcOfCircle CenterX=-16.5 CenterY=68 CenterZ=0 NormalX=0 NormalY=0 NormalZ=1 AngleXU=0 Radius=7.5 StartAngle=1.5708 EndAngle=2.97014
    g12: LineSegment StartX=-385 StartY=0 StartZ=0 EndX=-32.5 EndY=39 EndZ=0
  constraints (35):
    c: Vertical(g0)
    c: Coincident(g0,g1)
    c: Horizontal(g1)
    c: Coincident(g1,g2)
    c: Vertical(g2)
    c: Coincident(g3,g0)
    c: Coincident(g4,g1)
    c: Coincident(g3,g-4)
    c: Coincident(g4,g-3)
    c: Equal(g3,g4)
    c: DistanceX(g1,g1) = 65
    c: DistanceY(g0,g0) = 42
    c: Equal(g0,g2)
    c: PointOnObject(g8,g2)
    c: Coincident(g8,g2)
    c: Coincident(g9,g5)
    c: Vertical(g9,g5)
    c: Tangent(g6,g9) = 1.5708
    c: Tangent(g8,g6) = -1.5708
    c: Symmetric(g5,g5,g-2)
    c: DistanceY(g5,g1) = 5.5
    c: Radius(g9) = 7.5
    c: Radius(g8) = 4
    c: DistanceX(g5,g5) = 33
    c: PointOnObject(g10,g0)
    c: Coincident(g10,g0)
    c: Coincident(g11,g5)
    c: Vertical(g11,g5)
    c: Equal(g9,g11)
    c: Tangent(g11,g7) = -1.5708
    c: Equal(g8,g10)
    c: Tangent(g10,g7) = 1.5708
    c: Coincident(g12,g-4)
    c: Coincident(g12,g0)
    c: Equal(g3,g12)
FEATURE [Part::Extrusion] Extrude017
  Base = -> Sketch019
  Dir = (0,1,-2e-16)
  DirMode = 2
  FaceMakerClass = Part::FaceMakerBullseye
  LengthFwd = 135
  LengthRev = 0
  Solid = true
  Symmetric = false
FEATURE [Sketcher::SketchObject] Sketch017
  ExternalGeometry = -> [Extrude017]
  FullyConstrained = true
  MapMode = 5
  Placement = pos=(0,1.78e-14,81) rot=(0,0,1;0rad)
  Support = -> [Extrude017]
  sketch-geometry (7):
    g0: LineSegment StartX=-10 StartY=464.863 StartZ=0 EndX=10 EndY=464.863 EndZ=0
    g1: LineSegment StartX=10 StartY=464.863 StartZ=0 EndX=10 EndY=444.863 EndZ=0
    g2: LineSegment StartX=10 StartY=444.863 StartZ=0 EndX=-10 EndY=444.863 EndZ=0
    g3: LineSegment StartX=-10 StartY=444.863 StartZ=0 EndX=-10 EndY=464.863 EndZ=0
    g4: LineSegment StartX=-10 StartY=464.863 StartZ=0 EndX=-32.5 EndY=484.863 EndZ=0
    g5: LineSegment StartX=10 StartY=464.863 StartZ=0 EndX=32.5 EndY=484.863 EndZ=0
    g6: LineSegment StartX=10 StartY=454.863 StartZ=0 EndX=32.5 EndY=454.863 EndZ=0
  constraints (19):
    c: Coincident(g0,g1)
    c: Coincident(g1,g2)
    c: Coincident(g2,g3)
    c: Coincident(g3,g0)
    c: Horizontal(g0)
    c: Horizontal(g2)
    c: Vertical(g1)
    c: Vertical(g3)
    c: DistanceX(g2,g2) = 20
    c: DistanceY(g1,g1) = 20
    c: Coincident(g4,g0)
    c: Coincident(g5,g0)
    c: Coincident(g4,g-3)
    c: Coincident(g5,g-3)
    c: Equal(g4,g5)
    c: PointOnObject(g6,g1)
    c: Vertical(g5,g6)
    c: Symmetric(g1,g0,g6)
    c: DistanceY(g6,g5) = 30
FEATURE [Part::Extrusion] Extrude016
  Base = -> Sketch017
  Dir = (0,2e-16,1)
  DirMode = 2
  FaceMakerClass = Part::FaceMakerBullseye
  LengthFwd = 30
  LengthRev = 0
  Solid = true
  Symmetric = true
FEATURE [Part::Cut] Cut006  label="U069"
  Base = -> Extrude017
  Refine = true
  Tool = -> Extrude016
FEATURE [Part::Feature] BOLTS_part009  label="Circular hollow profile 508.0/10.0 l=360.0"
  Placement = pos=(0,0,-120) rot=(0,0,1;0rad)
  shape: bbox 508 x 508 x 360 mm, 4 faces (baked)
FEATURE [App::DocumentObjectGroup] Group007  label="R406_508_610"
  Group = -> [Cylinder001,Cut006,BooleanFragments004,BOLTS_part006,BOLTS_part007,BOLTS_part009]
FEATURE [TechDraw::DrawSVGTemplate] Template003
  EditableTexts = AUTHOR_NAME=Axians,DN=DN,DRAWING_TITLE=Leiterhalterung,FC-DATE=07.05.2021,FC-REV=REV A,FC-SC=1:5,FC-SH=X / Y,FC-SI=A3,+6 more (map truncated)
  Height = 297
  Orientation = 1
  Width = 420
FEATURE [TechDraw::DrawProjGroupItem] ProjItem009  label="Front003"
  CoarseView = false
  Direction = (0,1,0)
  Focus = 100
  HardHidden = true
  IsoCount = 0
  IsoHidden = false
  IsoVisible = false
  LockPosition = true
  Perspective = false
  Rotation = 0
  RotationVector = (-1,0,0)
  Scale = 0.2
  ScaleType = 2
  ScrubCount = 0
  SeamHidden = false
  SeamVisible = true
  SmoothHidden = false
  SmoothVisible = true
  Source = -> [Cut006,BooleanFragments004]
  Type = 0
  X = 0
  XDirection = (-1,0,0)
  Y = 0
FEATURE [TechDraw::DrawProjGroupItem] ProjItem010  label="Left003"
  CoarseView = false
  Direction = (1,1e-16,0)
  Focus = 100
  HardHidden = true
  IsoCount = 0
  IsoHidden = false
  IsoVisible = false
  LockPosition = false
  Perspective = false
  Rotation = 0
  RotationVector = (1,0,0)
  Scale = 0.2
  ScaleType = 2
  ScrubCount = 0
  SeamHidden = false
  SeamVisible = true
  SmoothHidden = false
  SmoothVisible = true
  Source = -> [Cut006,BooleanFragments004]
  Type = 1
  X = 116
  XDirection = (-1e-16,1,0)
  Y = 0
FEATURE [TechDraw::DrawProjGroupItem] ProjItem011  label="Top003"
  CoarseView = false
  Direction = (0,0,1)
  Focus = 100
  HardHidden = true
  IsoCount = 0
  IsoHidden = false
  IsoVisible = false
  LockPosition = false
  Perspective = false
  Rotation = 0
  RotationVector = (1,0,0)
  Scale = 0.2
  ScaleType = 2
  ScrubCount = 0
  SeamHidden = false
  SeamVisible = true
  SmoothHidden = false
  SmoothVisible = true
  Source = -> [Cut006,BooleanFragments004]
  Type = 4
  X = 0
  XDirection = (-1,0,0)
  Y = -51
FEATURE [TechDraw::DrawProjGroup] ProjGroup003
  Anchor = -> ProjItem009
  AutoDistribute = true
  LockPosition = false
  ProjectionType = 0
  Rotation = 0
  Scale = 0.2
  ScaleType = 2
  Source = -> [Cut006,BooleanFragments004]
  Views = -> [ProjItem009,ProjItem010,ProjItem011]
  X = 138.768
  Y = 203.634
  spacingX = 15
  spacingY = 15
FEATURE [TechDraw::DrawViewDimension] Dimension033
  AngleOverride = false
  Arbitrary = false
  ArbitraryTolerances = false
  EqualTolerance = true
  ExtensionAngle = 0
  FormatSpec = %.1f
  FormatSpecOverTolerance = %+.1f
  FormatSpecUnderTolerance = %+.1f
  Inverted = false
  LineAngle = 0
  LockPosition = false
  MeasureType = 1
  OverTolerance = 0
  References2D = -> [ProjItem009]
  Rotation = 0
  Scale = 0.2
  ScaleType = 2
  TheoreticalExact = false
  Type = 1
  UnderTolerance = 0
  X = -0.377373
  Y = 32.0601
FEATURE [TechDraw::DrawViewDimension] Dimension034
  AngleOverride = false
  Arbitrary = false
  ArbitraryTolerances = false
  EqualTolerance = true
  ExtensionAngle = 0
  FormatSpec = %.1f
  FormatSpecOverTolerance = %+.1f
  FormatSpecUnderTolerance = %+.1f
  Inverted = false
  LineAngle = 0
  LockPosition = false
  MeasureType = 1
  OverTolerance = 0
  References2D = -> [ProjItem009]
  Rotation = 0
  Scale = 0.2
  ScaleType = 2
  TheoreticalExact = false
  Type = 2
  UnderTolerance = 0
  X = -90.3913
  Y = 0.388155
FEATURE [TechDraw::DrawViewDimension] Dimension035
  AngleOverride = false
  Arbitrary = false
  ArbitraryTolerances = false
  EqualTolerance = true
  ExtensionAngle = 0
  FormatSpec = %.1f
  FormatSpecOverTolerance = %+.1f
  FormatSpecUnderTolerance = %+.1f
  Inverted = false
  LineAngle = 0
  LockPosition = false
  MeasureType = 1
  OverTolerance = 0
  References2D = -> [ProjItem010]
  Rotation = 0
  Scale = 0.2
  ScaleType = 2
  TheoreticalExact = false
  Type = 2
  UnderTolerance = 0
  X = -31.8249
  Y = 23.5494
FEATURE [TechDraw::DrawViewDimension] Dimension036
  AngleOverride = false
  Arbitrary = false
  ArbitraryTolerances = false
  EqualTolerance = true
  ExtensionAngle = 0
  FormatSpec = %.1f
  FormatSpecOverTolerance = %+.1f
  FormatSpecUnderTolerance = %+.1f
  Inverted = false
  LineAngle = 0
  LockPosition = false
  MeasureType = 1
  OverTolerance = 0
  References2D = -> [ProjItem010]
  Rotation = 0
  Scale = 0.2
  ScaleType = 2
  TheoreticalExact = false
  Type = 1
  UnderTolerance = 0
  X = -18.3781
  Y = 22.1871
FEATURE [TechDraw::DrawViewDimension] Dimension037
  AngleOverride = false
  Arbitrary = false
  ArbitraryTolerances = false
  EqualTolerance = true
  ExtensionAngle = 0
  FormatSpec = %.1f
  FormatSpecOverTolerance = %+.1f
  FormatSpecUnderTolerance = %+.1f
  Inverted = false
  LineAngle = 0
  LockPosition = false
  MeasureType = 1
  OverTolerance = 0
  References2D = -> [ProjItem009]
  Rotation = 0
  Scale = 0.2
  ScaleType = 2
  TheoreticalExact = false
  Type = 2
  UnderTolerance = 0
  X = -74.2275
  Y = 0.854397
FEATURE [TechDraw::DrawViewDimension] Dimension038
  AngleOverride = false
  Arbitrary = false
  ArbitraryTolerances = false
  EqualTolerance = true
  ExtensionAngle = 0
  FormatSpec = ⌀%.1f
  FormatSpecOverTolerance = %+.1f
  FormatSpecUnderTolerance = %+.1f
  Inverted = false
  LineAngle = 0
  LockPosition = false
  MeasureType = 1
  OverTolerance = 0
  References2D = -> [ProjItem009]
  Rotation = 0
  Scale = 0.2
  ScaleType = 2
  TheoreticalExact = false
  Type = 5
  UnderTolerance = 0
  X = 82.6177
  Y = 3.77373
FEATURE [TechDraw::DrawViewDimension] Dimension039
  AngleOverride = false
  Arbitrary = false
  ArbitraryTolerances = false
  EqualTolerance = true
  ExtensionAngle = 0
  FormatSpec = %.1f
  FormatSpecOverTolerance = %+.1f
  FormatSpecUnderTolerance = %+.1f
  Inverted = false
  LineAngle = 0
  LockPosition = false
  MeasureType = 1
  OverTolerance = 0
  References2D = -> [ProjItem009]
  Rotation = 0
  Scale = 0.2
  ScaleType = 2
  TheoreticalExact = false
  Type = 1
  UnderTolerance = 0
  X = -55.683
  Y = 1.96105
FEATURE [TechDraw::DrawViewDimension] Dimension040
  AngleOverride = false
  Arbitrary = false
  ArbitraryTolerances = false
  EqualTolerance = true
  ExtensionAngle = 0
  FormatSpec = %.1f
  FormatSpecOverTolerance = %+.1f
  FormatSpecUnderTolerance = %+.1f
  Inverted = false
  LineAngle = 0
  LockPosition = false
  MeasureType = 1
  OverTolerance = 0
  References2D = -> [ProjItem009]
  Rotation = 0
  Scale = 0.2
  ScaleType = 2
  TheoreticalExact = false
  Type = 1
  UnderTolerance = 0
  X = -31.8368
  Y = 19.2772
FEATURE [TechDraw::DrawViewDimension] Dimension041
  AngleOverride = false
  Arbitrary = false
  ArbitraryTolerances = false
  EqualTolerance = true
  ExtensionAngle = 0
  FormatSpec = %.1f
  FormatSpecOverTolerance = %+.1f
  FormatSpecUnderTolerance = %+.1f
  Inverted = false
  LineAngle = 0
  LockPosition = false
  MeasureType = 1
  OverTolerance = 0
  References2D = -> [ProjItem009]
  Rotation = 0
  Scale = 0.2
  ScaleType = 2
  TheoreticalExact = false
  Type = 1
  UnderTolerance = 0
  X = -67.8778
  Y = 23.7122
FEATURE [TechDraw::DrawViewDimension] Dimension042
  AngleOverride = false
  Arbitrary = false
  ArbitraryTolerances = false
  EqualTolerance = true
  ExtensionAngle = 0
  FormatSpec = %.1f
  FormatSpecOverTolerance = %+.1f
  FormatSpecUnderTolerance = %+.1f
  Inverted = false
  LineAngle = 0
  LockPosition = false
  MeasureType = 1
  OverTolerance = 0
  References2D = -> [ProjItem009]
  Rotation = 0
  Scale = 0.2
  ScaleType = 2
  TheoreticalExact = false
  Type = 1
  UnderTolerance = 0
  X = -0.404328
  Y = 25.7339
FEATURE [TechDraw::DrawViewDimension] Dimension043
  AngleOverride = false
  Arbitrary = false
  ArbitraryTolerances = false
  EqualTolerance = true
  ExtensionAngle = 0
  FormatSpec = %.1f
  FormatSpecOverTolerance = %+.1f
  FormatSpecUnderTolerance = %+.1f
  Inverted = false
  LineAngle = 0
  LockPosition = false
  MeasureType = 1
  OverTolerance = 0
  References2D = -> [ProjItem011]
  Rotation = 0
  Scale = 0.2
  ScaleType = 2
  TheoreticalExact = false
  Type = 2
  UnderTolerance = 0
  X = -95.0492
  Y = 17.9112
FEATURE [TechDraw::DrawViewDimension] Dimension044
  AngleOverride = false
  Arbitrary = false
  ArbitraryTolerances = false
  EqualTolerance = true
  ExtensionAngle = 0
  FormatSpec = %.1f
  FormatSpecOverTolerance = %+.1f
  FormatSpecUnderTolerance = %+.1f
  Inverted = false
  LineAngle = 0
  LockPosition = false
  MeasureType = 1
  OverTolerance = 0
  References2D = -> [ProjItem010]
  Rotation = 0
  Scale = 0.2
  ScaleType = 2
  TheoreticalExact = false
  Type = 1
  UnderTolerance = 0
  X = 9.80132
  Y = -21.6511
FEATURE [TechDraw::DrawViewDimension] Dimension045
  AngleOverride = false
  Arbitrary = false
  ArbitraryTolerances = false
  EqualTolerance = true
  ExtensionAngle = 0
  FormatSpec = %.1f
  FormatSpecOverTolerance = %+.1f
  FormatSpecUnderTolerance = %+.1f
  Inverted = false
  LineAngle = 0
  LockPosition = false
  MeasureType = 1
  OverTolerance = 0
  References2D = -> [ProjItem011]
  Rotation = 0
  Scale = 0.2
  ScaleType = 2
  TheoreticalExact = false
  Type = 2
  UnderTolerance = 0
  X = 19.0012
  Y = -6.35535
FEATURE [TechDraw::DrawViewDimension] Dimension046
  AngleOverride = false
  Arbitrary = false
  ArbitraryTolerances = false
  EqualTolerance = true
  ExtensionAngle = 0
  FormatSpec = %.1f
  FormatSpecOverTolerance = %+.1f
  FormatSpecUnderTolerance = %+.1f
  Inverted = false
  LineAngle = 0
  LockPosition = false
  MeasureType = 1
  OverTolerance = 0
  References2D = -> [ProjItem011]
  Rotation = 0
  Scale = 0.2
  ScaleType = 2
  TheoreticalExact = false
  Type = 6
  UnderTolerance = 0
  X = 70.9837
  Y = 30.2761
FEATURE [TechDraw::DrawViewDimension] Dimension047
  AngleOverride = false
  Arbitrary = false
  ArbitraryTolerances = false
  EqualTolerance = true
  ExtensionAngle = 0
  FormatSpec = %.1f
  FormatSpecOverTolerance = %+.1f
  FormatSpecUnderTolerance = %+.1f
  Inverted = false
  LineAngle = 0
  LockPosition = false
  MeasureType = 1
  OverTolerance = 0
  References2D = -> [ProjItem011]
  Rotation = 0
  Scale = 0.2
  ScaleType = 2
  TheoreticalExact = false
  Type = 1
  UnderTolerance = 0
  X = -0.0712
  Y = 21.5215
FEATURE [TechDraw::DrawViewDimension] Dimension048
  AngleOverride = false
  Arbitrary = false
  ArbitraryTolerances = false
  EqualTolerance = true
  ExtensionAngle = 0
  FormatSpec = %.1f
  FormatSpecOverTolerance = %+.1f
  FormatSpecUnderTolerance = %+.1f
  Inverted = false
  LineAngle = 0
  LockPosition = false
  MeasureType = 1
  OverTolerance = 0
  References2D = -> [ProjItem011]
  Rotation = 0
  Scale = 0.2
  ScaleType = 2
  TheoreticalExact = false
  Type = 1
  UnderTolerance = 0
  X = -41.1118
  Y = -6.22688
FEATURE [TechDraw::DrawViewBalloon] Balloon003
  BubbleShape = 0
  EndType = 0
  EndTypeScale = 1
  KinkLength = 5
  LockPosition = false
  OriginX = 94.1264
  OriginY = -11.7397
  Rotation = 0
  Scale = 0.2
  ScaleType = 2
  ShapeScale = 1
  SourceView = -> ProjItem010
  Text = 1
  TextWrapLen = -1
  X = 194.126
  Y = 88.2603
FEATURE [TechDraw::DrawViewAnnotation] Annotation003
  Font = Arial
  LineSpace = 80
  LockPosition = false
  MaxWidth = -1
  Rotation = 0
  Scale = 0.2
  ScaleType = 2
  Text = U-65
  TextSize = 5
  TextStyle = 0
  X = 323.588
  Y = 218.927
FEATURE [TechDraw::DrawPage] Page003  label="Page_R406_508_610"
  KeepUpdated = true
  NextBalloonIndex = 2
  ProjectionType = 0
  Template = -> Template003
  Views = -> [ProjGroup003,Dimension033,Dimension034,Dimension035,Dimension036,Dimension037,Dimension038,Dimension039,Dimension040,Dimension041,Dimension042,Dimension043,Dimension044,Dimension045,Dimension046,Dimension047,Dimension048,Balloon003,Annotation003]
FEATURE [Sketcher::SketchObject] Sketch022
  FullyConstrained = true
  sketch-geometry (10):
    g0: Circle CenterX=0 CenterY=0 CenterZ=0 NormalX=0 NormalY=0 NormalZ=1 AngleXU=0 Radius=457
    g1: LineSegment StartX=-244.451 StartY=390.254 StartZ=0 EndX=-30 EndY=490.254 EndZ=0
    g2: LineSegment StartX=30 StartY=490.254 StartZ=0 EndX=244.451 EndY=390.254 EndZ=0
    g3: LineSegment StartX=-30 StartY=490.254 StartZ=0 EndX=30 EndY=490.254 EndZ=0
    g4: LineSegment StartX=244.451 StartY=390.254 StartZ=0 EndX=525 EndY=390.254 EndZ=0
    g5: LineSegment StartX=525 StartY=390.254 StartZ=0 EndX=525 EndY=490.254 EndZ=0
    g6: LineSegment StartX=525 StartY=490.254 StartZ=0 EndX=30 EndY=490.254 EndZ=0
    g7: LineSegment StartX=-30 StartY=490.254 StartZ=0 EndX=-525 EndY=490.254 EndZ=0
    g8: LineSegment StartX=-525 StartY=490.254 StartZ=0 EndX=-525 EndY=390.254 EndZ=0
    g9: LineSegment StartX=-525 StartY=390.254 StartZ=0 EndX=-244.451 EndY=390.254 EndZ=0
  constraints (26):
    c: Coincident(g0,g-1)
    c: Tangent(g1,g0)
    c: Symmetric(g1,g2,g-2)
    c: Symmetric(g1,g2,g-2)
    c: Coincident(g3,g1)
    c: Coincident(g3,g2)
    c: Coincident(g2,g4)
    c: Horizontal(g4)
    c: Coincident(g4,g5)
    c: Vertical(g5)
    c: Coincident(g5,g6)
    c: Coincident(g6,g2)
    c: Horizontal(g6)
    c: Coincident(g1,g7)
    c: Horizontal(g7)
    c: Coincident(g7,g8)
    c: Vertical(g8)
    c: Coincident(g8,g9)
    c: Coincident(g9,g1)
    c: Horizontal(g9)
    c: Equal(g6,g7)
    c: Angle(g-1,g1) = 0.436332
    c: DistanceX(g3,g3) = 60
    c: Diameter(g0) = 914
    c: DistanceY(g5,g5) = 100
    c: DistanceX(g7,g5) = 1050
FEATURE [Part::Cylinder] Cylinder002
  Angle = 360
  AttacherType = Attacher::AttachEngine3D
  FirstAngle = 0
  Height = 600
  Placement = pos=(480,534.254,95) rot=(1,0,0;1.5708rad)
  Radius = 6
  SecondAngle = 0
FEATURE [Part::Extrusion] Extrude020  label="Eckblech009"
  Base = -> Sketch022
  Dir = (0,0,1)
  DirMode = 2
  FaceMakerClass = Part::FaceMakerBullseye
  LengthFwd = 10
  LengthRev = 0
  Solid = true
  Symmetric = false
FEATURE [Part::FeaturePython] Clone007  label="Eckblech008"  # Draft clone (typed FeaturePython)
  AttacherType = Attacher::AttachEngine3D
  Fuse = false
  Objects = -> [Extrude020]
  Placement = pos=(0,0,110) rot=(0,0,1;0rad)
  Scale = (1,1,1)
FEATURE [Sketcher::SketchObject] Sketch025
  ExternalGeometry = -> [Clone007,Extrude020]
  FullyConstrained = true
  MapMode = 5
  Placement = pos=(0,490.254,0) rot=(0,0.707107,0.707107;3.14159rad)
  Support = -> [Extrude020]
  sketch-geometry (4):
    g0: LineSegment StartX=-525 StartY=0 StartZ=0 EndX=525 EndY=0 EndZ=0
    g1: LineSegment StartX=525 StartY=0 StartZ=0 EndX=525 EndY=120 EndZ=0
    g2: LineSegment StartX=525 StartY=120 StartZ=0 EndX=-525 EndY=120 EndZ=0
    g3: LineSegment StartX=-525 StartY=120 StartZ=0 EndX=-525 EndY=0 EndZ=0
  constraints (10):
    c: Coincident(g0,g1)
    c: Coincident(g1,g2)
    c: Coincident(g2,g3)
    c: Coincident(g3,g0)
    c: Horizontal(g0)
    c: Horizontal(g2)
    c: Vertical(g1)
    c: Vertical(g3)
    c: Coincident(g0,g-4)
    c: Coincident(g1,g-3)
FEATURE [Part::Extrusion] Extrude023
  Base = -> Sketch025
  Dir = (0,1,-2e-16)
  DirMode = 2
  FaceMakerClass = Part::FaceMakerBullseye
  LengthFwd = 15
  LengthRev = 0
  Solid = true
  Symmetric = false
FEATURE [Sketcher::SketchObject] Sketch023
  ExternalGeometry = -> [Clone007,Extrude020]
  FullyConstrained = true
  MapMode = 5
  Placement = pos=(0,490.254,0) rot=(1,0,0;1.5708rad)
  Support = -> [Extrude023]
  sketch-geometry (36):
    g0: ArcOfCircle CenterX=-420 CenterY=95 CenterZ=0 NormalX=0 NormalY=0 NormalZ=1 AngleXU=0 Radius=7 StartAngle=1.5708 EndAngle=4.71239
    g1: ArcOfCircle CenterX=-365 CenterY=95 CenterZ=0 NormalX=0 NormalY=0 NormalZ=1 AngleXU=0 Radius=7 StartAngle=4.71239 EndAngle=7.85398
    g2: LineSegment StartX=-420 StartY=88 StartZ=0 EndX=-365 EndY=88 EndZ=0
    g3: LineSegment StartX=-420 StartY=102 StartZ=0 EndX=-365 EndY=102 EndZ=0
    g4: ArcOfCircle CenterX=365 CenterY=95 CenterZ=0 NormalX=0 NormalY=0 NormalZ=1 AngleXU=0 Radius=7 StartAngle=1.5708 EndAngle=4.71239
    g5: ArcOfCircle CenterX=420 CenterY=95 CenterZ=0 NormalX=0 NormalY=0 NormalZ=1 AngleXU=0 Radius=7 StartAngle=4.71239 EndAngle=7.85398
    g6: LineSegment StartX=365 StartY=88 StartZ=0 EndX=420 EndY=88 EndZ=0
    g7: LineSegment StartX=365 StartY=102 StartZ=0 EndX=420 EndY=102 EndZ=0
    g8: ArcOfCircle CenterX=-420 CenterY=25 CenterZ=0 NormalX=0 NormalY=0 NormalZ=1 AngleXU=0 Radius=7 StartAngle=1.5708 EndAngle=4.71239
    g9: ArcOfCircle CenterX=-365 CenterY=25 CenterZ=0 NormalX=0 NormalY=0 NormalZ=1 AngleXU=0 Radius=7 StartAngle=4.71239 EndAngle=7.85398
    g10: LineSegment StartX=-420 StartY=18 StartZ=0 EndX=-365 EndY=18 EndZ=0
    g11: LineSegment StartX=-420 StartY=32 StartZ=0 EndX=-365 EndY=32 EndZ=0
    g12: ArcOfCircle CenterX=365 CenterY=25 CenterZ=0 NormalX=0 NormalY=0 NormalZ=1 AngleXU=0 Radius=7 StartAngle=1.5708 EndAngle=4.71239
    g13: ArcOfCircle CenterX=420 CenterY=25 CenterZ=0 NormalX=0 NormalY=0 NormalZ=1 AngleXU=0 Radius=7 StartAngle=4.71239 EndAngle=7.85398
    g14: LineSegment StartX=365 StartY=18 StartZ=0 EndX=420 EndY=18 EndZ=0
    g15: LineSegment StartX=365 StartY=32 StartZ=0 EndX=420 EndY=32 EndZ=0
    g16: LineSegment StartX=-525 StartY=110 StartZ=0 EndX=-420 EndY=95 EndZ=0
    g17: LineSegment StartX=525 StartY=110 StartZ=0 EndX=420 EndY=95 EndZ=0
    g18: LineSegment StartX=-525 StartY=10 StartZ=0 EndX=-420 EndY=25 EndZ=0
    g19: ArcOfCircle CenterX=-420 CenterY=95 CenterZ=0 NormalX=0 NormalY=0 NormalZ=1 AngleXU=0 Radius=7 StartAngle=2e-16 EndAngle=1.5708
    g20: ArcOfCircle CenterX=-480 CenterY=95 CenterZ=0 NormalX=0 NormalY=0 NormalZ=1 AngleXU=0 Radius=7 StartAngle=1.5708 EndAngle=4.71239
    g21: ArcOfCircle CenterX=-465 CenterY=95 CenterZ=0 NormalX=0 NormalY=0 NormalZ=1 AngleXU=0 Radius=7 StartAngle=4.71239 EndAngle=7.85398
    g22: LineSegment StartX=-480 StartY=88 StartZ=0 EndX=-465 EndY=88 EndZ=0
    g23: LineSegment StartX=-480 StartY=102 StartZ=0 EndX=-465 EndY=102 EndZ=0
    g24: ArcOfCircle CenterX=-480 CenterY=25 CenterZ=0 NormalX=0 NormalY=0 NormalZ=1 AngleXU=0 Radius=7 StartAngle=1.5708 EndAngle=4.71239
    g25: ArcOfCircle CenterX=-465 CenterY=25 CenterZ=0 NormalX=0 NormalY=0 NormalZ=1 AngleXU=0 Radius=7 StartAngle=4.71239 EndAngle=7.85398
    g26: LineSegment StartX=-480 StartY=18 StartZ=0 EndX=-465 EndY=18 EndZ=0
    g27: LineSegment StartX=-480 StartY=32 StartZ=0 EndX=-465 EndY=32 EndZ=0
    g28: ArcOfCircle CenterX=465 CenterY=95 CenterZ=0 NormalX=0 NormalY=0 NormalZ=1 AngleXU=0 Radius=7 StartAngle=1.5708 EndAngle=4.71239
    g29: ArcOfCircle CenterX=480 CenterY=95 CenterZ=0 NormalX=0 NormalY=0 NormalZ=1 AngleXU=0 Radius=7 StartAngle=4.71239 EndAngle=7.85398
    g30: LineSegment StartX=465 StartY=88 StartZ=0 EndX=480 EndY=88 EndZ=0
    g31: LineSegment StartX=465 StartY=102 StartZ=0 EndX=480 EndY=102 EndZ=0
    g32: ArcOfCircle CenterX=465 CenterY=25 CenterZ=0 NormalX=0 NormalY=0 NormalZ=1 AngleXU=0 Radius=7 StartAngle=1.5708 EndAngle=4.71239
    g33: ArcOfCircle CenterX=480 CenterY=25 CenterZ=0 NormalX=0 NormalY=0 NormalZ=1 AngleXU=0 Radius=7 StartAngle=4.71239 EndAngle=7.85398
    g34: LineSegment StartX=465 StartY=18 StartZ=0 EndX=480 EndY=18 EndZ=0
    g35: LineSegment StartX=465 StartY=32 StartZ=0 EndX=480 EndY=32 EndZ=0
  constraints (85):
    c: Tangent(g0,g3) = 1.5708
    c: Tangent(g2,g1) = -1.5708
    c: Tangent(g3,g1) = 1.5708
    c: Equal(g0,g1)
    c: Tangent(g4,g7) = 1.5708
    c: Tangent(g4,g6) = -1.5708
    c: Tangent(g6,g5) = -1.5708
    c: Tangent(g7,g5) = 1.5708
    c: Horizontal(g6)
    c: Equal(g4,g5)
    c: Tangent(g8,g11) = 1.5708
    c: Tangent(g8,g10) = -1.5708
    c: Tangent(g10,g9) = -1.5708
    c: Tangent(g11,g9) = 1.5708
    c: Horizontal(g10)
    c: Equal(g8,g9)
    c: Tangent(g12,g15) = 1.5708
    c: Tangent(g12,g14) = -1.5708
    c: Tangent(g14,g13) = -1.5708
    c: Tangent(g15,g13) = 1.5708
    c: Horizontal(g14)
    c: Equal(g12,g13)
    c: Symmetric(g1,g4,g-2)
    c: Symmetric(g9,g12,g-2)
    c: Vertical(g1,g9)
    c: Equal(g9,g1)
    c: Equal(g1,g4)
    c: Equal(g4,g12)
    c: Equal(g3,g11)
    c: Equal(g11,g7)
    c: Equal(g7,g15)
    c: Diameter(g0) = 14
    c: Coincident(g16,g-4)
    c: Coincident(g16,g0)
    c: Coincident(g17,g-3)
    c: Coincident(g17,g5)
    c: DistanceY(g8,g0) = 70
    c: Tangent(g0,g2) = -1.5708
    c: Horizontal(g2)
    c: Coincident(g18,g-6)
    c: Coincident(g18,g8)
    c: Equal(g16,g18)
    c: Coincident(g19,g0)
    c: Coincident(g19,g0)
    c: Horizontal(g19,g0)
    c: DistanceX(g3,g3) = 55
    c: Tangent(g20,g23) = 1.5708
    c: Tangent(g20,g22) = -1.5708
    c: Tangent(g22,g21) = -1.5708
    c: Tangent(g23,g21) = 1.5708
    c: Horizontal(g22)
    c: Equal(g20,g21)
    c: Tangent(g24,g27) = 1.5708
    c: Tangent(g24,g26) = -1.5708
    c: Tangent(g26,g25) = -1.5708
    c: Tangent(g27,g25) = 1.5708
    c: Horizontal(g26)
    c: Equal(g24,g25)
    c: Tangent(g28,g31) = 1.5708
    c: Tangent(g28,g30) = -1.5708
    c: Tangent(g30,g29) = -1.5708
    c: Tangent(g31,g29) = 1.5708
    c: Horizontal(g30)
    c: Equal(g28,g29)
    c: Tangent(g32,g35) = 1.5708
    c: Tangent(g32,g34) = -1.5708
    c: Tangent(g34,g33) = -1.5708
    c: Tangent(g35,g33) = 1.5708
    c: Horizontal(g34)
    c: Equal(g32,g33)
    c: Equal(g22,g27)
    c: Equal(g27,g30)
    c: Equal(g30,g35)
    c: Equal(g0,g21)
    c: Equal(g21,g25)
    c: Equal(g25,g28)
    c: Equal(g28,g32)
    c: Symmetric(g28,g21,g-2)
    c: Horizontal(g21,g0)
    c: Symmetric(g32,g25,g-2)
    c: Vertical(g21,g25)
    c: DistanceX(g22,g22) = 15
    c: Horizontal(g25,g8)
    c: DistanceX(g13,g32) = 45
    c: DistanceX(g1,g4) = 730
FEATURE [Sketcher::SketchObject] Sketch024
  ExternalGeometry = -> [Extrude023]
  FullyConstrained = true
  MapMode = 5
  Placement = pos=(0,505.254,0) rot=(0,0.707107,0.707107;3.14159rad)
  Support = -> [Extrude023]
  sketch-geometry (13):
    g0: LineSegment StartX=-32.5 StartY=39 StartZ=0 EndX=-32.5 EndY=81 EndZ=0
    g1: LineSegment StartX=-32.5 StartY=81 StartZ=0 EndX=32.5 EndY=81 EndZ=0
    g2: LineSegment StartX=32.5 StartY=81 StartZ=0 EndX=32.5 EndY=39 EndZ=0
    g3: LineSegment StartX=-32.5 StartY=81 StartZ=0 EndX=-525 EndY=120 EndZ=0
    g4: LineSegment StartX=32.5 StartY=81 StartZ=0 EndX=525 EndY=120 EndZ=0
    g5: LineSegment StartX=-16.5 StartY=75.5 StartZ=0 EndX=16.5 EndY=75.5 EndZ=0
    g6: LineSegment StartX=23.89 StartY=69.2796 StartZ=0 EndX=28.5586 EndY=42.3175 EndZ=0
    g7: LineSegment StartX=-23.89 StartY=69.2796 StartZ=0 EndX=-28.5586 EndY=42.3175 EndZ=0
    g8: ArcOfCircle CenterX=32.5 CenterY=43 CenterZ=0 NormalX=0 NormalY=0 NormalZ=1 AngleXU=0 Radius=4 StartAngle=3.31305 EndAngle=4.71239
    g9: ArcOfCircle CenterX=16.5 CenterY=68 CenterZ=0 NormalX=0 NormalY=0 NormalZ=1 AngleXU=0 Radius=7.5 StartAngle=0.171455 EndAngle=1.5708
    g10: ArcOfCircle CenterX=-32.5 CenterY=43 CenterZ=0 NormalX=0 NormalY=0 NormalZ=1 AngleXU=0 Radius=4 StartAngle=4.71239 EndAngle=6.11173
    g11: ArcOfCircle CenterX=-16.5 CenterY=68 CenterZ=0 NormalX=0 NormalY=0 NormalZ=1 AngleXU=0 Radius=7.5 StartAngle=1.5708 EndAngle=2.97014
    g12: LineSegment StartX=-525 StartY=0 StartZ=0 EndX=-32.5 EndY=39 EndZ=0
  constraints (35):
    c: Vertical(g0)
    c: Coincident(g0,g1)
    c: Horizontal(g1)
    c: Coincident(g1,g2)
    c: Vertical(g2)
    c: Coincident(g3,g0)
    c: Coincident(g4,g1)
    c: Coincident(g3,g-4)
    c: Coincident(g4,g-3)
    c: Equal(g3,g4)
    c: DistanceX(g1,g1) = 65
    c: DistanceY(g0,g0) = 42
    c: Equal(g0,g2)
    c: PointOnObject(g8,g2)
    c: Coincident(g8,g2)
    c: Coincident(g9,g5)
    c: Vertical(g9,g5)
    c: Tangent(g6,g9) = 1.5708
    c: Tangent(g8,g6) = -1.5708
    c: Symmetric(g5,g5,g-2)
    c: DistanceY(g5,g1) = 5.5
    c: Radius(g9) = 7.5
    c: Radius(g8) = 4
    c: DistanceX(g5,g5) = 33
    c: PointOnObject(g10,g0)
    c: Coincident(g10,g0)
    c: Coincident(g11,g5)
    c: Vertical(g11,g5)
    c: Equal(g9,g11)
    c: Tangent(g11,g7) = -1.5708
    c: Equal(g8,g10)
    c: Tangent(g10,g7) = 1.5708
    c: Coincident(g12,g-4)
    c: Coincident(g12,g0)
    c: Equal(g3,g12)
FEATURE [Part::Extrusion] Extrude022
  Base = -> Sketch024
  Dir = (0,1,-2e-16)
  DirMode = 2
  FaceMakerClass = Part::FaceMakerBullseye
  LengthFwd = 135
  LengthRev = 0
  Solid = true
  Symmetric = false
FEATURE [Sketcher::SketchObject] Sketch021
  ExternalGeometry = -> [Extrude022]
  FullyConstrained = true
  MapMode = 5
  Placement = pos=(0,1.78e-14,81) rot=(0,0,1;0rad)
  Support = -> [Extrude022]
  sketch-geometry (7):
    g0: LineSegment StartX=-10 StartY=620.254 StartZ=0 EndX=10 EndY=620.254 EndZ=0
    g1: LineSegment StartX=10 StartY=620.254 StartZ=0 EndX=10 EndY=600.254 EndZ=0
    g2: LineSegment StartX=10 StartY=600.254 StartZ=0 EndX=-10 EndY=600.254 EndZ=0
    g3: LineSegment StartX=-10 StartY=600.254 StartZ=0 EndX=-10 EndY=620.254 EndZ=0
    g4: LineSegment StartX=-10 StartY=620.254 StartZ=0 EndX=-32.5 EndY=640.254 EndZ=0
    g5: LineSegment StartX=10 StartY=620.254 StartZ=0 EndX=32.5 EndY=640.254 EndZ=0
    g6: LineSegment StartX=10 StartY=610.254 StartZ=0 EndX=32.5 EndY=610.254 EndZ=0
  constraints (19):
    c: Coincident(g0,g1)
    c: Coincident(g1,g2)
    c: Coincident(g2,g3)
    c: Coincident(g3,g0)
    c: Horizontal(g0)
    c: Horizontal(g2)
    c: Vertical(g1)
    c: Vertical(g3)
    c: DistanceX(g2,g2) = 20
    c: DistanceY(g1,g1) = 20
    c: Coincident(g4,g0)
    c: Coincident(g5,g0)
    c: Coincident(g4,g-3)
    c: Coincident(g5,g-3)
    c: Equal(g4,g5)
    c: PointOnObject(g6,g1)
    c: Vertical(g5,g6)
    c: Symmetric(g1,g0,g6)
    c: DistanceY(g6,g5) = 30
FEATURE [Part::Extrusion] Extrude021
  Base = -> Sketch021
  Dir = (0,2e-16,1)
  DirMode = 2
  FaceMakerClass = Part::FaceMakerBullseye
  LengthFwd = 30
  LengthRev = 0
  Solid = true
  Symmetric = true
FEATURE [Part::Cut] Cut008  label="U070"
  Base = -> Extrude022
  Refine = true
  Tool = -> Extrude021
FEATURE [Part::Extrusion] Extrude024
  Base = -> Sketch023
  Dir = (0,1,0)
  DirMode = 0
  FaceMakerClass = Part::FaceMakerBullseye
  LengthFwd = 50
  LengthRev = 0
  Solid = true
  Symmetric = true
FEATURE [Part::Cut] Cut009
  Base = -> Extrude023
  Refine = true
  Tool = -> Extrude024
FEATURE [Part::FeaturePython] BooleanFragments005  label="BooleanFragments006"  # WARN: FeaturePython — macro-defined, semantics opaque (R4)
  Mode = 0
  Objects = -> [Extrude020,Clone007,Cut009]
  Tolerance = 0
FEATURE [Part::Feature] BOLTS_part010  label="Circular hollow profile 711.0/10.0 l=360.0"
  Placement = pos=(0,0,-120) rot=(0,0,1;0rad)
  shape: bbox 711 x 711 x 360 mm, 4 faces (baked)
FEATURE [Part::Feature] BOLTS_part011  label="Circular hollow profile 762.0/10.0 l=360.0"
  Placement = pos=(0,0,-120) rot=(0,0,1;0rad)
  shape: bbox 762 x 762 x 360 mm, 4 faces (baked)
FEATURE [Part::Feature] BOLTS_part012  label="Circular hollow profile 813.0/10.0 l=360.0"
  Placement = pos=(0,0,-120) rot=(0,0,1;0rad)
  shape: bbox 813 x 813 x 360 mm, 4 faces (baked)
FEATURE [App::DocumentObjectGroup] Group  label="R711_762_813_914"
  Group = -> [BOLTS_part008,Cylinder002,BooleanFragments005,BOLTS_part010,BOLTS_part011,BOLTS_part012,Cut008]
FEATURE [TechDraw::DrawSVGTemplate] Template004
  EditableTexts = AUTHOR_NAME=Axians,DN=DN,DRAWING_TITLE=Leiterhalterung,FC-DATE=07.05.2021,FC-REV=REV A,FC-SC=1:5,FC-SH=X / Y,FC-SI=A3,+6 more (map truncated)
  Height = 297
  Orientation = 1
  Width = 420
FEATURE [TechDraw::DrawProjGroupItem] ProjItem012  label="Front004"
  CoarseView = false
  Direction = (0,1,0)
  Focus = 100
  HardHidden = true
  IsoCount = 0
  IsoHidden = false
  IsoVisible = false
  LockPosition = true
  Perspective = false
  Rotation = 0
  RotationVector = (-1,0,0)
  Scale = 0.2
  ScaleType = 2
  ScrubCount = 0
  SeamHidden = false
  SeamVisible = true
  SmoothHidden = false
  SmoothVisible = true
  Source = -> [BooleanFragments005,Cut008]
  Type = 0
  X = 0
  XDirection = (-1,0,0)
  Y = 0
FEATURE [TechDraw::DrawProjGroupItem] ProjItem013  label="Left004"
  CoarseView = false
  Direction = (1,1e-16,0)
  Focus = 100
  HardHidden = true
  IsoCount = 0
  IsoHidden = false
  IsoVisible = false
  LockPosition = false
  Perspective = false
  Rotation = 0
  RotationVector = (1,0,0)
  Scale = 0.2
  ScaleType = 2
  ScrubCount = 0
  SeamHidden = false
  SeamVisible = true
  SmoothHidden = false
  SmoothVisible = true
  Source = -> [BooleanFragments005,Cut008]
  Type = 1
  X = 145
  XDirection = (-1e-16,1,0)
  Y = 0
FEATURE [TechDraw::DrawProjGroupItem] ProjItem014  label="Top004"
  CoarseView = false
  Direction = (0,0,1)
  Focus = 100
  HardHidden = true
  IsoCount = 0
  IsoHidden = false
  IsoVisible = false
  LockPosition = false
  Perspective = false
  Rotation = 0
  RotationVector = (1,0,0)
  Scale = 0.2
  ScaleType = 2
  ScrubCount = 0
  SeamHidden = false
  SeamVisible = true
  SmoothHidden = false
  SmoothVisible = true
  Source = -> [BooleanFragments005,Cut008]
  Type = 4
  X = 0
  XDirection = (-1,0,0)
  Y = -52
FEATURE [TechDraw::DrawProjGroup] ProjGroup004
  Anchor = -> ProjItem012
  AutoDistribute = true
  LockPosition = false
  ProjectionType = 0
  Rotation = 0
  Scale = 0.2
  ScaleType = 2
  Source = -> [BooleanFragments005,Cut008]
  Views = -> [ProjItem012,ProjItem013,ProjItem014]
  X = 151.244
  Y = 237.037
  spacingX = 15
  spacingY = 15
FEATURE [TechDraw::DrawViewBalloon] Balloon004
  BubbleShape = 0
  EndType = 0
  EndTypeScale = 1
  KinkLength = 5
  LockPosition = false
  OriginX = 100.366
  OriginY = -6.03659
  Rotation = 0
  Scale = 0.2
  ScaleType = 2
  ShapeScale = 1
  SourceView = -> ProjItem013
  Text = 1
  TextWrapLen = -1
  X = 200.366
  Y = 93.9634
FEATURE [TechDraw::DrawViewAnnotation] Annotation004
  Font = Arial
  LineSpace = 80
  LockPosition = false
  MaxWidth = -1
  Rotation = 0
  Scale = 0.2
  ScaleType = 2
  Text = U-65
  TextSize = 5
  TextStyle = 0
  X = 371.78
  Y = 254.744
FEATURE [TechDraw::DrawViewDimension] Dimension049
  AngleOverride = false
  Arbitrary = false
  ArbitraryTolerances = false
  EqualTolerance = true
  ExtensionAngle = 0
  FormatSpec = %.1f
  FormatSpecOverTolerance = %+.1f
  FormatSpecUnderTolerance = %+.1f
  Inverted = false
  LineAngle = 0
  LockPosition = false
  MeasureType = 1
  OverTolerance = 0
  References2D = -> [ProjItem012]
  Rotation = 0
  Scale = 0.2
  ScaleType = 2
  TheoreticalExact = false
  Type = 1
  UnderTolerance = 0
  X = 0.425202
  Y = 26.6695
FEATURE [TechDraw::DrawViewDimension] Dimension050
  AngleOverride = false
  Arbitrary = false
  ArbitraryTolerances = false
  EqualTolerance = true
  ExtensionAngle = 0
  FormatSpec = %.1f
  FormatSpecOverTolerance = %+.1f
  FormatSpecUnderTolerance = %+.1f
  Inverted = false
  LineAngle = 0
  LockPosition = false
  MeasureType = 1
  OverTolerance = 0
  References2D = -> [ProjItem012]
  Rotation = 0
  Scale = 0.2
  ScaleType = 2
  TheoreticalExact = false
  Type = 2
  UnderTolerance = 0
  X = -120.945
  Y = 0
FEATURE [TechDraw::DrawViewDimension] Dimension051
  AngleOverride = false
  Arbitrary = false
  ArbitraryTolerances = false
  EqualTolerance = true
  ExtensionAngle = 0
  FormatSpec = %.1f
  FormatSpecOverTolerance = %+.1f
  FormatSpecUnderTolerance = %+.1f
  Inverted = false
  LineAngle = 0
  LockPosition = false
  MeasureType = 1
  OverTolerance = 0
  References2D = -> [ProjItem014]
  Rotation = 0
  Scale = 0.2
  ScaleType = 2
  TheoreticalExact = false
  Type = 2
  UnderTolerance = 0
  X = -117.118
  Y = 14.5748
FEATURE [TechDraw::DrawViewDimension] Dimension052
  AngleOverride = false
  Arbitrary = false
  ArbitraryTolerances = false
  EqualTolerance = true
  ExtensionAngle = 0
  FormatSpec = %.1f
  FormatSpecOverTolerance = %+.1f
  FormatSpecUnderTolerance = %+.1f
  Inverted = false
  LineAngle = 0
  LockPosition = false
  MeasureType = 1
  OverTolerance = 0
  References2D = -> [ProjItem013]
  Rotation = 0
  Scale = 0.2
  ScaleType = 2
  TheoreticalExact = false
  Type = 2
  UnderTolerance = 0
  X = -36.2313
  Y = 18.9742
FEATURE [TechDraw::DrawViewDimension] Dimension053
  AngleOverride = false
  Arbitrary = false
  ArbitraryTolerances = false
  EqualTolerance = true
  ExtensionAngle = 0
  FormatSpec = %.1f
  FormatSpecOverTolerance = %+.1f
  FormatSpecUnderTolerance = %+.1f
  Inverted = false
  LineAngle = 0
  LockPosition = false
  MeasureType = 1
  OverTolerance = 0
  References2D = -> [ProjItem013]
  Rotation = 0
  Scale = 0.2
  ScaleType = 2
  TheoreticalExact = false
  Type = 1
  UnderTolerance = 0
  X = -17.0899
  Y = 18.1772
FEATURE [TechDraw::DrawViewDimension] Dimension054
  AngleOverride = false
  Arbitrary = false
  ArbitraryTolerances = false
  EqualTolerance = true
  ExtensionAngle = 0
  FormatSpec = %.1f
  FormatSpecOverTolerance = %+.1f
  FormatSpecUnderTolerance = %+.1f
  Inverted = false
  LineAngle = 0
  LockPosition = false
  MeasureType = 1
  OverTolerance = 0
  References2D = -> [ProjItem013]
  Rotation = 0
  Scale = 0.2
  ScaleType = 2
  TheoreticalExact = false
  Type = 1
  UnderTolerance = 0
  X = 11.8882
  Y = -25.1604
FEATURE [TechDraw::DrawViewDimension] Dimension055
  AngleOverride = false
  Arbitrary = false
  ArbitraryTolerances = false
  EqualTolerance = true
  ExtensionAngle = 0
  FormatSpec = %.1f
  FormatSpecOverTolerance = %+.1f
  FormatSpecUnderTolerance = %+.1f
  Inverted = false
  LineAngle = 0
  LockPosition = false
  MeasureType = 1
  OverTolerance = 0
  References2D = -> [ProjItem014]
  Rotation = 0
  Scale = 0.2
  ScaleType = 2
  TheoreticalExact = false
  Type = 2
  UnderTolerance = 0
  X = 15.6941
  Y = -33.5325
FEATURE [TechDraw::DrawViewDimension] Dimension056
  AngleOverride = false
  Arbitrary = false
  ArbitraryTolerances = false
  EqualTolerance = true
  ExtensionAngle = 0
  FormatSpec = %.1f
  FormatSpecOverTolerance = %+.1f
  FormatSpecUnderTolerance = %+.1f
  Inverted = false
  LineAngle = 0
  LockPosition = false
  MeasureType = 1
  OverTolerance = 0
  References2D = -> [ProjItem014]
  Rotation = 0
  Scale = 0.2
  ScaleType = 2
  TheoreticalExact = false
  Type = 6
  UnderTolerance = 0
  X = 88.6835
  Y = 32.9776
FEATURE [TechDraw::DrawViewDimension] Dimension057
  AngleOverride = false
  Arbitrary = false
  ArbitraryTolerances = false
  EqualTolerance = true
  ExtensionAngle = 0
  FormatSpec = %.1f
  FormatSpecOverTolerance = %+.1f
  FormatSpecUnderTolerance = %+.1f
  Inverted = false
  LineAngle = 0
  LockPosition = false
  MeasureType = 1
  OverTolerance = 0
  References2D = -> [ProjItem014]
  Rotation = 0
  Scale = 0.2
  ScaleType = 2
  TheoreticalExact = false
  Type = 1
  UnderTolerance = 0
  X = -0.259985
  Y = 22.9389
FEATURE [TechDraw::DrawViewDimension] Dimension058
  AngleOverride = false
  Arbitrary = false
  ArbitraryTolerances = false
  EqualTolerance = true
  ExtensionAngle = 0
  FormatSpec = %.1f
  FormatSpecOverTolerance = %+.1f
  FormatSpecUnderTolerance = %+.1f
  Inverted = false
  LineAngle = 0
  LockPosition = false
  MeasureType = 1
  OverTolerance = 0
  References2D = -> [ProjItem014]
  Rotation = 0
  Scale = 0.2
  ScaleType = 2
  TheoreticalExact = false
  Type = 1
  UnderTolerance = 0
  X = -56.0589
  Y = -10.9299
FEATURE [TechDraw::DrawViewDimension] Dimension059
  AngleOverride = false
  Arbitrary = false
  ArbitraryTolerances = false
  EqualTolerance = true
  ExtensionAngle = 0
  FormatSpec = %.1f
  FormatSpecOverTolerance = %+.1f
  FormatSpecUnderTolerance = %+.1f
  Inverted = false
  LineAngle = 0
  LockPosition = false
  MeasureType = 1
  OverTolerance = 0
  References2D = -> [ProjItem012]
  Rotation = 0
  Scale = 0.2
  ScaleType = 2
  TheoreticalExact = false
  Type = 1
  UnderTolerance = 0
  X = -88.2047
  Y = 20.5829
FEATURE [TechDraw::DrawViewDimension] Dimension060
  AngleOverride = false
  Arbitrary = false
  ArbitraryTolerances = false
  EqualTolerance = true
  ExtensionAngle = 0
  FormatSpec = %.1f
  FormatSpecOverTolerance = %+.1f
  FormatSpecUnderTolerance = %+.1f
  Inverted = false
  LineAngle = 0
  LockPosition = false
  MeasureType = 1
  OverTolerance = 0
  References2D = -> [ProjItem012]
  Rotation = 0
  Scale = 0.2
  ScaleType = 2
  TheoreticalExact = false
  Type = 1
  UnderTolerance = 0
  X = -0.708671
  Y = 20.6419
FEATURE [TechDraw::DrawViewDimension] Dimension061
  AngleOverride = false
  Arbitrary = false
  ArbitraryTolerances = false
  EqualTolerance = true
  ExtensionAngle = 0
  FormatSpec = %.1f
  FormatSpecOverTolerance = %+.1f
  FormatSpecUnderTolerance = %+.1f
  Inverted = false
  LineAngle = 0
  LockPosition = false
  MeasureType = 1
  OverTolerance = 0
  References2D = -> [ProjItem012]
  Rotation = 0
  Scale = 0.2
  ScaleType = 2
  TheoreticalExact = false
  Type = 1
  UnderTolerance = 0
  X = 84.7558
  Y = 3.11965
FEATURE [TechDraw::DrawViewDimension] Dimension062
  AngleOverride = false
  Arbitrary = false
  ArbitraryTolerances = false
  EqualTolerance = true
  ExtensionAngle = 0
  FormatSpec = %.1f
  FormatSpecOverTolerance = %+.1f
  FormatSpecUnderTolerance = %+.1f
  Inverted = false
  LineAngle = 0
  LockPosition = false
  MeasureType = 1
  OverTolerance = 0
  References2D = -> [ProjItem012]
  Rotation = 0
  Scale = 0.2
  ScaleType = 2
  TheoreticalExact = false
  Type = 1
  UnderTolerance = 0
  X = 61.6691
  Y = 0.600869
FEATURE [TechDraw::DrawViewDimension] Dimension063
  AngleOverride = false
  Arbitrary = false
  ArbitraryTolerances = false
  EqualTolerance = true
  ExtensionAngle = 0
  FormatSpec = %.1f
  FormatSpecOverTolerance = %+.1f
  FormatSpecUnderTolerance = %+.1f
  Inverted = false
  LineAngle = 0
  LockPosition = false
  MeasureType = 1
  OverTolerance = 0
  References2D = -> [ProjItem012]
  Rotation = 0
  Scale = 0.2
  ScaleType = 2
  TheoreticalExact = false
  Type = 2
  UnderTolerance = 0
  X = -101.669
  Y = 0.708671
FEATURE [TechDraw::DrawViewDimension] Dimension064
  AngleOverride = false
  Arbitrary = false
  ArbitraryTolerances = false
  EqualTolerance = true
  ExtensionAngle = 0
  FormatSpec = ⌀%.1f
  FormatSpecOverTolerance = %+.1f
  FormatSpecUnderTolerance = %+.1f
  Inverted = false
  LineAngle = 0
  LockPosition = false
  MeasureType = 1
  OverTolerance = 0
  References2D = -> [ProjItem012]
  Rotation = 0
  Scale = 0.2
  ScaleType = 2
  TheoreticalExact = false
  Type = 5
  UnderTolerance = 0
  X = -61.1228
  Y = -0.708671
FEATURE [TechDraw::DrawPage] Page004
  KeepUpdated = true
  NextBalloonIndex = 2
  ProjectionType = 0
  Template = -> Template004
  Views = -> [ProjGroup004,Balloon004,Annotation004,Dimension049,Dimension050,Dimension051,Dimension052,Dimension053,Dimension054,Dimension055,Dimension056,Dimension057,Dimension058,Dimension059,Dimension060,Dimension061,Dimension062,Dimension063,Dimension064]
FEATURE [Part::Feature] BOLTS_part013  label="Circular hollow profile 139.7/6.3 l=360.001"
  Placement = pos=(0,49,-120) rot=(0,0,1;0rad)
  shape: bbox 139.7 x 139.7 x 360 mm, 4 faces (baked)
FEATURE [Part::FeaturePython] Clone008  label="U071"  # Draft clone (typed FeaturePython)
  AttacherType = Attacher::AttachEngine3D
  Fuse = false
  Objects = -> [Cut002]
  Scale = (1,1,1)
FEATURE [Part::FeaturePython] Clone009  label="Eckblech010"  # Draft clone (typed FeaturePython)
  AttacherType = Attacher::AttachEngine3D
  Fuse = false
  Objects = -> [Extrude005]
  Scale = (1,1,1)
FEATURE [Part::FeaturePython] Clone010  label="Eckblech011"  # Draft clone (typed FeaturePython)
  AttacherType = Attacher::AttachEngine3D
  Fuse = false
  Objects = -> [Clone004]
  Placement = pos=(0,0,110) rot=(0,0,1;0rad)
  Scale = (1,1,1)
FEATURE [Part::FeaturePython] Clone011  label="Cut010"  # Draft clone (typed FeaturePython)
  AttacherType = Attacher::AttachEngine3D
  Fuse = false
  Objects = -> [Cut003]
  Scale = (1,1,1)
FEATURE [Part::Cut] Cut010  label="Cut011"
  Base = -> Clone009
  Refine = true
  Tool = -> BOLTS_part013
FEATURE [Part::Cut] Cut011  label="Cut012"
  Base = -> Clone010
  Refine = true
  Tool = -> BOLTS_part013
FEATURE [Part::MultiFuse] Fusion
  Refine = true
  Shapes = -> [Clone008,Clone011,Cut010,Cut011]
FEATURE [Fem::FemMeshObjectPython] FEMMeshGmsh  # FEM object (typed FeaturePython)
  Algorithm2D = 0
  Algorithm3D = 0
  CharacteristicLengthMax = 5
  CharacteristicLengthMin = 0
  CoherenceMesh = true
  ElementDimension = 3
  ElementOrder = 1
  GeometryTolerance = 1e-06
  GroupsOfNodes = false
  HighOrderOptimize = 0
  MeshSizeFromCurvature = 12
  OptimizeNetgen = false
  OptimizeStd = true
  Part = -> Fusion
  RecombinationAlgorithm = 0
  Recombine3DAll = false
  RecombineAll = false
  SecondOrderLinear = false
FEATURE [Fem::FemSolverObjectPython] SolverCcxTools  # FEM object (typed FeaturePython)
  AnalysisType = 0
  BeamShellResultOutput3D = true
  BucklingFactors = 1
  EigenmodeHighLimit = 1000000
  EigenmodeLowLimit = 0
  EigenmodesCount = 10
  GeometricalNonlinearity = 0
  IterationsControlParameterCutb = 0.25,0.5,0.75,0.85,,,1.5,
  IterationsControlParameterIter = 4,8,9,200,10,400,,200,,
  IterationsControlParameterTimeUse = false
  IterationsThermoMechMaximum = 2000
  IterationsUserDefinedIncrementations = false
  IterationsUserDefinedTimeStepLength = false
  MaterialNonlinearity = 0
  MatrixSolverType = 0
  SplitInputWriter = true
  ThermoMechSteadyState = true
  TimeEnd = 1
  TimeInitialStep = 0.01
FEATURE [App::MaterialObjectPython] MaterialSolid  label="S355"  # material (typed FeaturePython)
  Category = 0
  Material = AuthorAndLicense=(c) 2013 Juergen Riegel (CC-BY 3.0),CardName=CalculiX-Steel,Density=7900 kg/m^3,+8 more (map truncated)
FEATURE [Fem::ConstraintFixed] ConstraintFixed
  NormalDirection = (0.573576,-0.819152,0)
  Normals = (36) [(0.478338,-0.878176,0),(0.573576,-0.819152,0),(0.661614,-0.749845,0),(0.478338,-0.878176,0),(0.573576,-0.819152,0),(0.661614,-0.749845,0),+30 more]
  Points = (36) [(-33.4119,110.341,120),(-40.0643,106.218,120),(-46.2137,101.377,120),(-33.4119,110.341,115),(-40.0643,106.218,115),(-46.2137,101.377,115),+30 more]
  References = -> [Fusion]
FEATURE [Fem::ConstraintForce] ConstraintForce
  Direction = -> Fusion [Edge109]
  DirectionVector = (0,0,-1)
  Force = 6000
  NormalDirection = (1,0,0)
  Points = (36) [(-10,241.482,75.5),(-10,231.482,75.5),(-10,221.482,75.5),(-10,241.482,78.25),(-10,231.482,78.25),(-10,221.482,78.25),(-10,241.482,81),+29 more]
  References = -> [Fusion]
  Reversed = true
FEATURE [Fem::ConstraintForce] ConstraintForce001
  Direction = -> Fusion [Edge102]
  DirectionVector = (0,-1,2e-16)
  Force = 20000
  NormalDirection = (-1,0,2e-16)
  Points = (18) [(120,136.482,68),(127,136.482,75),(120,136.482,82),(120,128.982,68),(127,128.982,75),(120,128.982,82),(120,121.482,68),(127,121.482,75),+10 more]
  References = -> [Fusion]
  Reversed = true
FEATURE [Fem::FemAnalysis] Analysis
  Group = -> [SolverCcxTools,MaterialSolid,ConstraintFixed,ConstraintForce,ConstraintForce001,FEMMeshGmsh]
FEATURE [Part::Feature] Part__Feature  label="leiter"
  Placement = pos=(-6e-14,271,-478) rot=(0,0,1;1.5708rad)
  shape: bbox 382 x 52 x 1200 mm, 62 faces (baked)
